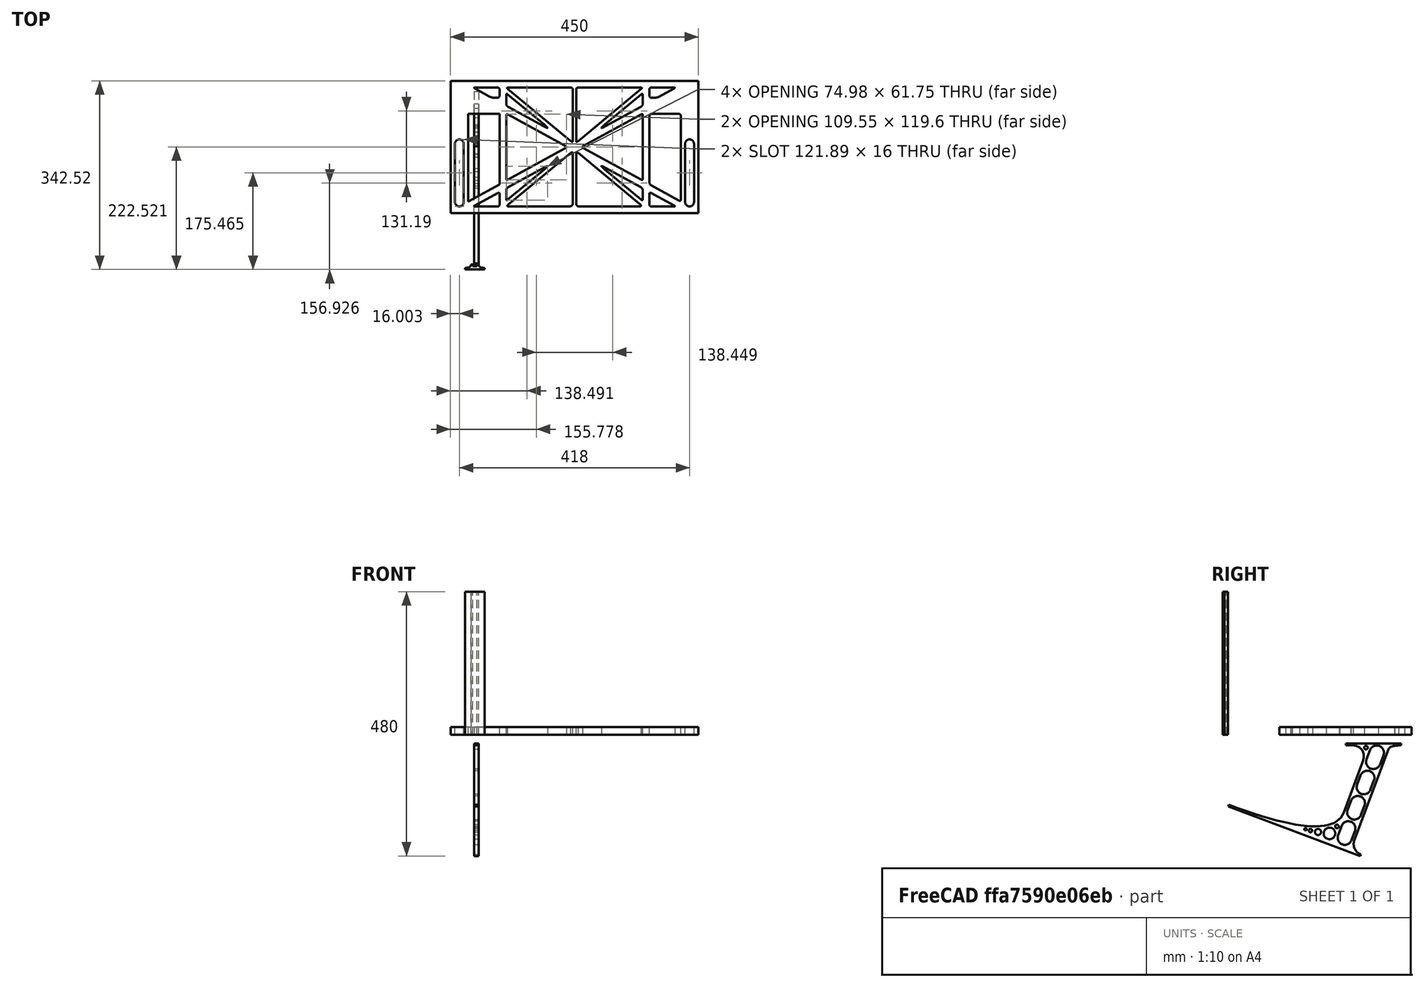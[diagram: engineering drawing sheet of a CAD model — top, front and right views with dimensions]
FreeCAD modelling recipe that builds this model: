
FCSTD DOCUMENT  (FreeCAD 0.19R0.19.2)
Label: laptopStand147FCStd
License: All rights reserved
LicenseURL: http://en.wikipedia.org/wiki/All_rights_reserved
objects: Sketcher::SketchObject×4, Part::Extrusion×3
note: 7 computed .brp shape members not serialized (recipe doc carries the construction recipe); baked Part::Feature solids carry a one-line shape summary decoded from their .brp

FEATURE [Sketcher::SketchObject] Sketch
  FullyConstrained = false
  sketch-geometry (349):
    g0: LineSegment StartX=-10.9272 StartY=-82.7794 StartZ=0 EndX=46.0728 EndY=-51.4823 EndZ=0
    g1: LineSegment StartX=-10.9272 StartY=76.4095 StartZ=0 EndX=-10.9272 EndY=-82.7794 EndZ=0
    g2: LineSegment StartX=46.0728 StartY=76.4095 StartZ=0 EndX=46.0728 EndY=-51.4823 EndZ=0
    g3: LineSegment StartX=-42.9272 StartY=136.221 StartZ=0 EndX=-42.9272 EndY=-103.779 EndZ=0
    g4: LineSegment StartX=407.073 StartY=136.221 StartZ=0 EndX=407.073 EndY=-103.779 EndZ=0
    g5: ArcOfCircle CenterX=-26.9272 CenterY=-83.7794 CenterZ=0 NormalX=0 NormalY=0 NormalZ=1 AngleXU=0 Radius=8 StartAngle=3.14159 EndAngle=6.28319
    g6: ArcOfCircle CenterX=391.073 CenterY=22.1087 CenterZ=0 NormalX=0 NormalY=0 NormalZ=1 AngleXU=0 Radius=8 StartAngle=-4.4e-15 EndAngle=3.14159
    g7: LineSegment StartX=399.073 StartY=22.1087 StartZ=0 EndX=399.073 EndY=-83.7794 EndZ=0
    g8: LineSegment StartX=383.073 StartY=22.1087 StartZ=0 EndX=383.073 EndY=-83.7794 EndZ=0
    g9: ArcOfCircle CenterX=391.073 CenterY=-83.7794 CenterZ=0 NormalX=0 NormalY=0 NormalZ=1 AngleXU=0 Radius=8 StartAngle=3.14159 EndAngle=6.28319
    g10: Circle CenterX=175.022 CenterY=27.0628 CenterZ=0 NormalX=0 NormalY=0 NormalZ=1 AngleXU=0 Radius=1
    g11: Circle CenterX=179.022 CenterY=24.8665 CenterZ=0 NormalX=0 NormalY=0 NormalZ=1 AngleXU=0 Radius=1
    g12: Circle CenterX=179.022 CenterY=27.0628 CenterZ=0 NormalX=0 NormalY=0 NormalZ=1 AngleXU=0 Radius=1
    g13: BSplineCurve PolesCount=3 KnotsCount=2 Degree=2 IsPeriodic=0
    g14: GeomPoint X=175.022 Y=27.0628 Z=0
    g15: GeomPoint X=179.022 Y=27.0628 Z=0
    g16: Circle CenterX=189.124 CenterY=27.0628 CenterZ=0 NormalX=0 NormalY=0 NormalZ=1 AngleXU=0 Radius=1
    g17: Circle CenterX=185.124 CenterY=24.8665 CenterZ=0 NormalX=0 NormalY=0 NormalZ=1 AngleXU=0 Radius=1
    g18: Circle CenterX=185.124 CenterY=27.0628 CenterZ=0 NormalX=0 NormalY=0 NormalZ=1 AngleXU=0 Radius=1
    g19: BSplineCurve PolesCount=3 KnotsCount=2 Degree=2 IsPeriodic=0
    g20: GeomPoint X=189.124 Y=27.0628 Z=0
    g21: GeomPoint X=185.124 Y=27.0628 Z=0
    g22: Circle CenterX=175.022 CenterY=5.37834 CenterZ=0 NormalX=0 NormalY=0 NormalZ=1 AngleXU=0 Radius=1
    g23: Circle CenterX=179.022 CenterY=7.57463 CenterZ=0 NormalX=0 NormalY=0 NormalZ=1 AngleXU=0 Radius=1
    g24: Circle CenterX=179.022 CenterY=5.34704 CenterZ=0 NormalX=0 NormalY=0 NormalZ=1 AngleXU=0 Radius=1
    g25: BSplineCurve PolesCount=3 KnotsCount=2 Degree=2 IsPeriodic=0
    g26: GeomPoint X=175.022 Y=5.37834 Z=0
    g27: GeomPoint X=179.022 Y=5.34704 Z=0
    g28: Circle CenterX=189.124 CenterY=5.37834 CenterZ=0 NormalX=0 NormalY=0 NormalZ=1 AngleXU=0 Radius=1
    g29: Circle CenterX=185.124 CenterY=7.57463 CenterZ=0 NormalX=0 NormalY=0 NormalZ=1 AngleXU=0 Radius=1
    g30: Circle CenterX=185.124 CenterY=5.34704 CenterZ=0 NormalX=0 NormalY=0 NormalZ=1 AngleXU=0 Radius=1
    g31: BSplineCurve PolesCount=3 KnotsCount=2 Degree=2 IsPeriodic=0
    g32: GeomPoint X=189.124 Y=5.37834 Z=0
    g33: GeomPoint X=185.124 Y=5.34704 Z=0
    g34: Circle CenterX=165.871 CenterY=18.1458 CenterZ=0 NormalX=0 NormalY=0 NormalZ=1 AngleXU=0 Radius=1
    g35: Circle CenterX=169.377 CenterY=16.2206 CenterZ=0 NormalX=0 NormalY=0 NormalZ=1 AngleXU=0 Radius=1
    g36: Circle CenterX=165.871 CenterY=14.2954 CenterZ=0 NormalX=0 NormalY=0 NormalZ=1 AngleXU=0 Radius=1
    g37: BSplineCurve PolesCount=3 KnotsCount=2 Degree=2 IsPeriodic=0
    g38: GeomPoint X=165.871 Y=18.1458 Z=0
    g39: GeomPoint X=165.871 Y=14.2954 Z=0
    g40: Circle CenterX=198.275 CenterY=18.1458 CenterZ=0 NormalX=0 NormalY=0 NormalZ=1 AngleXU=0 Radius=1
    g41: Circle CenterX=194.768 CenterY=16.2206 CenterZ=0 NormalX=0 NormalY=0 NormalZ=1 AngleXU=0 Radius=1
    g42: Circle CenterX=198.275 CenterY=14.2954 CenterZ=0 NormalX=0 NormalY=0 NormalZ=1 AngleXU=0 Radius=1
    g43: BSplineCurve PolesCount=3 KnotsCount=2 Degree=2 IsPeriodic=0
    g44: GeomPoint X=198.275 Y=18.1458 Z=0
    g45: GeomPoint X=198.275 Y=14.2954 Z=0
    g46: LineSegment StartX=407.073 StartY=-103.779 StartZ=0 EndX=-42.9272 EndY=-103.779 EndZ=0
    g47: LineSegment StartX=407.073 StartY=136.221 StartZ=0 EndX=-42.9272 EndY=136.221 EndZ=0
    g48: LineSegment StartX=46.0728 StartY=76.4095 StartZ=0 EndX=-10.9272 EndY=76.4095 EndZ=0
    g49: Circle CenterX=125.607 CenterY=54.1951 CenterZ=0 NormalX=0 NormalY=0 NormalZ=1 AngleXU=0 Radius=1
    g50: Circle CenterX=139.632 CenterY=46.4944 CenterZ=0 NormalX=0 NormalY=0 NormalZ=1 AngleXU=0 Radius=1
    g51: Circle CenterX=127.326 CenterY=56.7187 CenterZ=0 NormalX=0 NormalY=0 NormalZ=1 AngleXU=0 Radius=1
    g52: BSplineCurve PolesCount=3 KnotsCount=2 Degree=2 IsPeriodic=0
    g53: GeomPoint X=125.607 Y=54.1951 Z=0
    g54: GeomPoint X=127.326 Y=56.7187 Z=0
    g55: Circle CenterX=236.821 CenterY=56.7187 CenterZ=0 NormalX=0 NormalY=0 NormalZ=1 AngleXU=0 Radius=1
    g56: Circle CenterX=224.513 CenterY=46.4944 CenterZ=0 NormalX=0 NormalY=0 NormalZ=1 AngleXU=0 Radius=1
    g57: Circle CenterX=238.538 CenterY=54.1951 CenterZ=0 NormalX=0 NormalY=0 NormalZ=1 AngleXU=0 Radius=1
    g58: BSplineCurve PolesCount=3 KnotsCount=2 Degree=2 IsPeriodic=0
    g59: GeomPoint X=236.821 Y=56.7187 Z=0
    g60: GeomPoint X=238.538 Y=54.1951 Z=0
    g61: Circle CenterX=238.538 CenterY=-21.7539 CenterZ=0 NormalX=0 NormalY=0 NormalZ=1 AngleXU=0 Radius=1
    g62: Circle CenterX=224.513 CenterY=-14.0532 CenterZ=0 NormalX=0 NormalY=0 NormalZ=1 AngleXU=0 Radius=1
    g63: Circle CenterX=236.821 CenterY=-24.2775 CenterZ=0 NormalX=0 NormalY=0 NormalZ=1 AngleXU=0 Radius=1
    g64: BSplineCurve PolesCount=3 KnotsCount=2 Degree=2 IsPeriodic=0
    g65: GeomPoint X=238.538 Y=-21.7539 Z=0
    g66: GeomPoint X=236.821 Y=-24.2775 Z=0
    g67: Circle CenterX=125.607 CenterY=-21.7539 CenterZ=0 NormalX=0 NormalY=0 NormalZ=1 AngleXU=0 Radius=1
    g68: Circle CenterX=139.632 CenterY=-14.0532 CenterZ=0 NormalX=0 NormalY=0 NormalZ=1 AngleXU=0 Radius=1
    g69: Circle CenterX=127.325 CenterY=-24.2775 CenterZ=0 NormalX=0 NormalY=0 NormalZ=1 AngleXU=0 Radius=1
    g70: BSplineCurve PolesCount=3 KnotsCount=2 Degree=2 IsPeriodic=0
    g71: GeomPoint X=125.607 Y=-21.7539 Z=0
    g72: GeomPoint X=127.325 Y=-24.2775 Z=0
    g73: Circle CenterX=302.996 CenterY=111.695 CenterZ=0 NormalX=0 NormalY=0 NormalZ=1 AngleXU=0 Radius=1
    g74: Circle CenterX=306.073 CenterY=114.251 CenterZ=0 NormalX=0 NormalY=0 NormalZ=1 AngleXU=0 Radius=1
    g75: Circle CenterX=306.073 CenterY=110.251 CenterZ=0 NormalX=0 NormalY=0 NormalZ=1 AngleXU=0 Radius=1
    g76: BSplineCurve PolesCount=3 KnotsCount=2 Degree=2 IsPeriodic=0
    g77: GeomPoint X=302.996 Y=111.695 Z=0
    g78: GeomPoint X=306.073 Y=110.251 Z=0
    g79: Circle CenterX=306.073 CenterY=95.2763 CenterZ=0 NormalX=0 NormalY=0 NormalZ=1 AngleXU=0 Radius=1
    g80: Circle CenterX=306.073 CenterY=91.2763 CenterZ=0 NormalX=0 NormalY=0 NormalZ=1 AngleXU=0 Radius=1
    g81: Circle CenterX=302.567 CenterY=89.3511 CenterZ=0 NormalX=0 NormalY=0 NormalZ=1 AngleXU=0 Radius=1
    g82: BSplineCurve PolesCount=3 KnotsCount=2 Degree=2 IsPeriodic=0
    g83: GeomPoint X=306.073 Y=95.2763 Z=0
    g84: GeomPoint X=302.567 Y=89.3511 Z=0
    g85: LineSegment StartX=306.073 StartY=110.251 StartZ=0 EndX=306.073 EndY=95.2763 EndZ=0
    g86: LineSegment StartX=302.996 StartY=111.695 StartZ=0 EndX=236.821 EndY=56.7187 EndZ=0
    g87: LineSegment StartX=238.538 StartY=54.1951 StartZ=0 EndX=302.567 EndY=89.3511 EndZ=0
    g88: Circle CenterX=61.1496 CenterY=111.695 CenterZ=0 NormalX=0 NormalY=0 NormalZ=1 AngleXU=0 Radius=1
    g89: Circle CenterX=58.0728 CenterY=114.251 CenterZ=0 NormalX=0 NormalY=0 NormalZ=1 AngleXU=0 Radius=1
    g90: Circle CenterX=58.0728 CenterY=110.251 CenterZ=0 NormalX=0 NormalY=0 NormalZ=1 AngleXU=0 Radius=1
    g91: BSplineCurve PolesCount=3 KnotsCount=2 Degree=2 IsPeriodic=0
    g92: GeomPoint X=61.1496 Y=111.695 Z=0
    g93: GeomPoint X=58.0728 Y=110.251 Z=0
    g94: Circle CenterX=61.5791 CenterY=89.3511 CenterZ=0 NormalX=0 NormalY=0 NormalZ=1 AngleXU=0 Radius=1
    g95: Circle CenterX=58.0728 CenterY=91.2763 CenterZ=0 NormalX=0 NormalY=0 NormalZ=1 AngleXU=0 Radius=1
    g96: Circle CenterX=58.0728 CenterY=95.2763 CenterZ=0 NormalX=0 NormalY=0 NormalZ=1 AngleXU=0 Radius=1
    g97: BSplineCurve PolesCount=3 KnotsCount=2 Degree=2 IsPeriodic=0
    g98: GeomPoint X=61.5791 Y=89.3511 Z=0
    g99: GeomPoint X=58.0728 Y=95.2763 Z=0
    g100: LineSegment StartX=58.0728 StartY=110.251 StartZ=0 EndX=58.0728 EndY=95.2763 EndZ=0
    g101: LineSegment StartX=61.1496 StartY=111.695 StartZ=0 EndX=127.326 EndY=56.7187 EndZ=0
    g102: LineSegment StartX=125.607 StartY=54.1951 StartZ=0 EndX=61.5791 EndY=89.3511 EndZ=0
    g103: Circle CenterX=61.5791 CenterY=-56.9099 CenterZ=0 NormalX=0 NormalY=0 NormalZ=1 AngleXU=0 Radius=1
    g104: Circle CenterX=58.0728 CenterY=-58.8351 CenterZ=0 NormalX=0 NormalY=0 NormalZ=1 AngleXU=0 Radius=1
    g105: Circle CenterX=58.0728 CenterY=-62.8351 CenterZ=0 NormalX=0 NormalY=0 NormalZ=1 AngleXU=0 Radius=1
    g106: BSplineCurve PolesCount=3 KnotsCount=2 Degree=2 IsPeriodic=0
    g107: GeomPoint X=61.5791 Y=-56.9099 Z=0
    g108: GeomPoint X=58.0728 Y=-62.8351 Z=0
    g109: Circle CenterX=58.0728 CenterY=-77.8102 CenterZ=0 NormalX=0 NormalY=0 NormalZ=1 AngleXU=0 Radius=1
    g110: Circle CenterX=58.0728 CenterY=-81.8102 CenterZ=0 NormalX=0 NormalY=0 NormalZ=1 AngleXU=0 Radius=1
    g111: Circle CenterX=61.1496 CenterY=-79.2541 CenterZ=0 NormalX=0 NormalY=0 NormalZ=1 AngleXU=0 Radius=1
    g112: BSplineCurve PolesCount=3 KnotsCount=2 Degree=2 IsPeriodic=0
    g113: GeomPoint X=58.0728 Y=-77.8102 Z=0
    g114: GeomPoint X=61.1496 Y=-79.2541 Z=0
    g115: LineSegment StartX=58.0728 StartY=-62.8351 StartZ=0 EndX=58.0728 EndY=-77.8102 EndZ=0
    g116: LineSegment StartX=61.1496 StartY=-79.2541 StartZ=0 EndX=127.325 EndY=-24.2775 EndZ=0
    g117: LineSegment StartX=125.607 StartY=-21.7539 StartZ=0 EndX=61.5791 EndY=-56.9099 EndZ=0
    g118: Circle CenterX=302.567 CenterY=-56.9099 CenterZ=0 NormalX=0 NormalY=0 NormalZ=1 AngleXU=0 Radius=1
    g119: Circle CenterX=306.073 CenterY=-58.8351 CenterZ=0 NormalX=0 NormalY=0 NormalZ=1 AngleXU=0 Radius=1
    g120: Circle CenterX=306.073 CenterY=-62.8351 CenterZ=0 NormalX=0 NormalY=0 NormalZ=1 AngleXU=0 Radius=1
    g121: BSplineCurve PolesCount=3 KnotsCount=2 Degree=2 IsPeriodic=0
    g122: GeomPoint X=302.567 Y=-56.9099 Z=0
    g123: GeomPoint X=306.073 Y=-62.8351 Z=0
    g124: Circle CenterX=302.996 CenterY=-79.2541 CenterZ=0 NormalX=0 NormalY=0 NormalZ=1 AngleXU=0 Radius=1
    g125: Circle CenterX=306.073 CenterY=-81.8102 CenterZ=0 NormalX=0 NormalY=0 NormalZ=1 AngleXU=0 Radius=1
    g126: Circle CenterX=306.073 CenterY=-77.8102 CenterZ=0 NormalX=0 NormalY=0 NormalZ=1 AngleXU=0 Radius=1
    g127: BSplineCurve PolesCount=3 KnotsCount=2 Degree=2 IsPeriodic=0
    g128: GeomPoint X=302.996 Y=-79.2541 Z=0
    g129: GeomPoint X=306.073 Y=-77.8102 Z=0
    g130: LineSegment StartX=306.073 StartY=-62.8351 StartZ=0 EndX=306.073 EndY=-77.8102 EndZ=0
    g131: LineSegment StartX=302.996 StartY=-79.2541 StartZ=0 EndX=236.821 EndY=-24.2775 EndZ=0
    g132: LineSegment StartX=238.538 StartY=-21.7539 StartZ=0 EndX=302.567 EndY=-56.9099 EndZ=0
    g133: Circle CenterX=61.6457 CenterY=-88.8112 CenterZ=0 NormalX=0 NormalY=0 NormalZ=1 AngleXU=0 Radius=1
    g134: Circle CenterX=58.0728 CenterY=-91.7794 CenterZ=0 NormalX=0 NormalY=0 NormalZ=1 AngleXU=0 Radius=1
    g135: Circle CenterX=63.9135 CenterY=-91.7794 CenterZ=0 NormalX=0 NormalY=0 NormalZ=1 AngleXU=0 Radius=1
    g136: BSplineCurve PolesCount=3 KnotsCount=2 Degree=2 IsPeriodic=0
    g137: GeomPoint X=61.6457 Y=-88.8112 Z=0
    g138: GeomPoint X=63.9135 Y=-91.7794 Z=0
    g139: Circle CenterX=179.022 CenterY=-85.8163 CenterZ=0 NormalX=0 NormalY=0 NormalZ=1 AngleXU=0 Radius=1
    g140: Circle CenterX=179.022 CenterY=-91.7794 CenterZ=0 NormalX=0 NormalY=0 NormalZ=1 AngleXU=0 Radius=1
    g141: Circle CenterX=171.895 CenterY=-91.7794 CenterZ=0 NormalX=0 NormalY=0 NormalZ=1 AngleXU=0 Radius=1
    g142: BSplineCurve PolesCount=3 KnotsCount=2 Degree=2 IsPeriodic=0
    g143: GeomPoint X=179.022 Y=-85.8163 Z=0
    g144: GeomPoint X=171.895 Y=-91.7794 Z=0
    g145: Circle CenterX=185.124 CenterY=-86.2028 CenterZ=0 NormalX=0 NormalY=0 NormalZ=1 AngleXU=0 Radius=1
    g146: Circle CenterX=185.124 CenterY=-91.7794 CenterZ=0 NormalX=0 NormalY=0 NormalZ=1 AngleXU=0 Radius=1
    g147: Circle CenterX=191.747 CenterY=-91.7794 CenterZ=0 NormalX=0 NormalY=0 NormalZ=1 AngleXU=0 Radius=1
    g148: BSplineCurve PolesCount=3 KnotsCount=2 Degree=2 IsPeriodic=0
    g149: GeomPoint X=185.124 Y=-86.2028 Z=0
    g150: GeomPoint X=191.747 Y=-91.7794 Z=0
    g151: Circle CenterX=299.888 CenterY=-86.6413 CenterZ=0 NormalX=0 NormalY=0 NormalZ=1 AngleXU=0 Radius=1
    g152: Circle CenterX=306.073 CenterY=-91.7794 CenterZ=0 NormalX=0 NormalY=0 NormalZ=1 AngleXU=0 Radius=1
    g153: Circle CenterX=298.776 CenterY=-91.7794 CenterZ=0 NormalX=0 NormalY=0 NormalZ=1 AngleXU=0 Radius=1
    g154: BSplineCurve PolesCount=3 KnotsCount=2 Degree=2 IsPeriodic=0
    g155: GeomPoint X=299.888 Y=-86.6413 Z=0
    g156: GeomPoint X=298.776 Y=-91.7794 Z=0
    g157: LineSegment StartX=189.124 StartY=5.37834 StartZ=0 EndX=299.888 EndY=-86.6413 EndZ=0
    g158: LineSegment StartX=298.776 StartY=-91.7794 StartZ=0 EndX=191.747 EndY=-91.7794 EndZ=0
    g159: LineSegment StartX=185.124 StartY=-86.2028 StartZ=0 EndX=185.124 EndY=5.34704 EndZ=0
    g160: LineSegment StartX=179.022 StartY=5.34704 StartZ=0 EndX=179.022 EndY=-85.8163 EndZ=0
    g161: LineSegment StartX=171.895 StartY=-91.7794 StartZ=0 EndX=63.9135 EndY=-91.7794 EndZ=0
    g162: LineSegment StartX=61.6457 StartY=-88.8112 StartZ=0 EndX=175.022 EndY=5.37834 EndZ=0
    g163: Circle CenterX=302.073 CenterY=124.221 CenterZ=0 NormalX=0 NormalY=0 NormalZ=1 AngleXU=0 Radius=1
    g164: Circle CenterX=306.073 CenterY=124.221 CenterZ=0 NormalX=0 NormalY=0 NormalZ=1 AngleXU=0 Radius=1
    g165: Circle CenterX=302.996 CenterY=121.665 CenterZ=0 NormalX=0 NormalY=0 NormalZ=1 AngleXU=0 Radius=1
    g166: BSplineCurve PolesCount=3 KnotsCount=2 Degree=2 IsPeriodic=0
    g167: GeomPoint X=302.073 Y=124.221 Z=0
    g168: GeomPoint X=302.996 Y=121.665 Z=0
    g169: Circle CenterX=189.124 CenterY=124.221 CenterZ=0 NormalX=0 NormalY=0 NormalZ=1 AngleXU=0 Radius=1
    g170: Circle CenterX=185.124 CenterY=124.221 CenterZ=0 NormalX=0 NormalY=0 NormalZ=1 AngleXU=0 Radius=1
    g171: Circle CenterX=185.124 CenterY=120.221 CenterZ=0 NormalX=0 NormalY=0 NormalZ=1 AngleXU=0 Radius=1
    g172: BSplineCurve PolesCount=3 KnotsCount=2 Degree=2 IsPeriodic=0
    g173: GeomPoint X=189.124 Y=124.221 Z=0
    g174: GeomPoint X=185.124 Y=120.221 Z=0
    g175: Circle CenterX=175.022 CenterY=124.221 CenterZ=0 NormalX=0 NormalY=0 NormalZ=1 AngleXU=0 Radius=1
    g176: Circle CenterX=179.022 CenterY=124.221 CenterZ=0 NormalX=0 NormalY=0 NormalZ=1 AngleXU=0 Radius=1
    g177: Circle CenterX=179.022 CenterY=120.221 CenterZ=0 NormalX=0 NormalY=0 NormalZ=1 AngleXU=0 Radius=1
    g178: BSplineCurve PolesCount=3 KnotsCount=2 Degree=2 IsPeriodic=0
    g179: GeomPoint X=175.022 Y=124.221 Z=0
    g180: GeomPoint X=179.022 Y=120.221 Z=0
    g181: Circle CenterX=62.0728 CenterY=124.221 CenterZ=0 NormalX=0 NormalY=0 NormalZ=1 AngleXU=0 Radius=1
    g182: Circle CenterX=58.0728 CenterY=124.221 CenterZ=0 NormalX=0 NormalY=0 NormalZ=1 AngleXU=0 Radius=1
    g183: Circle CenterX=61.1496 CenterY=121.665 CenterZ=0 NormalX=0 NormalY=0 NormalZ=1 AngleXU=0 Radius=1
    g184: BSplineCurve PolesCount=3 KnotsCount=2 Degree=2 IsPeriodic=0
    g185: GeomPoint X=62.0728 Y=124.221 Z=0
    g186: GeomPoint X=61.1496 Y=121.665 Z=0
    g187: LineSegment StartX=62.0728 StartY=124.221 StartZ=0 EndX=175.022 EndY=124.221 EndZ=0
    g188: LineSegment StartX=179.022 StartY=120.221 StartZ=0 EndX=179.022 EndY=27.0628 EndZ=0
    g189: LineSegment StartX=185.124 StartY=27.0628 StartZ=0 EndX=185.124 EndY=120.221 EndZ=0
    g190: LineSegment StartX=189.124 StartY=124.221 StartZ=0 EndX=302.073 EndY=124.221 EndZ=0
    g191: LineSegment StartX=302.996 StartY=121.665 StartZ=0 EndX=189.124 EndY=27.0628 EndZ=0
    g192: LineSegment StartX=175.022 StartY=27.0628 StartZ=0 EndX=61.1496 EndY=121.665 EndZ=0
    g193: Circle CenterX=61.5791 CenterY=75.4095 CenterZ=0 NormalX=0 NormalY=0 NormalZ=1 AngleXU=0 Radius=1
    g194: Circle CenterX=58.0728 CenterY=77.3346 CenterZ=0 NormalX=0 NormalY=0 NormalZ=1 AngleXU=0 Radius=1
    g195: Circle CenterX=58.0728 CenterY=73.3346 CenterZ=0 NormalX=0 NormalY=0 NormalZ=1 AngleXU=0 Radius=1
    g196: BSplineCurve PolesCount=3 KnotsCount=2 Degree=2 IsPeriodic=0
    g197: GeomPoint X=61.5791 Y=75.4095 Z=0
    g198: GeomPoint X=58.0728 Y=73.3346 Z=0
    g199: Circle CenterX=58.0728 CenterY=-40.8935 CenterZ=0 NormalX=0 NormalY=0 NormalZ=1 AngleXU=0 Radius=1
    g200: Circle CenterX=58.0728 CenterY=-44.8935 CenterZ=0 NormalX=0 NormalY=0 NormalZ=1 AngleXU=0 Radius=1
    g201: Circle CenterX=61.5791 CenterY=-42.9683 CenterZ=0 NormalX=0 NormalY=0 NormalZ=1 AngleXU=0 Radius=1
    g202: BSplineCurve PolesCount=3 KnotsCount=2 Degree=2 IsPeriodic=0
    g203: GeomPoint X=58.0728 Y=-40.8935 Z=0
    g204: GeomPoint X=61.5791 Y=-42.9683 Z=0
    g205: LineSegment StartX=61.5791 StartY=-42.9683 StartZ=0 EndX=165.871 EndY=14.2954 EndZ=0
    g206: LineSegment StartX=165.871 StartY=18.1458 StartZ=0 EndX=61.5791 EndY=75.4095 EndZ=0
    g207: LineSegment StartX=58.0728 StartY=73.3346 StartZ=0 EndX=58.0728 EndY=-40.8935 EndZ=0
    g208: Circle CenterX=302.567 CenterY=-42.9683 CenterZ=0 NormalX=0 NormalY=0 NormalZ=1 AngleXU=0 Radius=1
    g209: Circle CenterX=306.073 CenterY=-44.8935 CenterZ=0 NormalX=0 NormalY=0 NormalZ=1 AngleXU=0 Radius=1
    g210: Circle CenterX=306.073 CenterY=-40.8935 CenterZ=0 NormalX=0 NormalY=0 NormalZ=1 AngleXU=0 Radius=1
    g211: BSplineCurve PolesCount=3 KnotsCount=2 Degree=2 IsPeriodic=0
    g212: GeomPoint X=302.567 Y=-42.9683 Z=0
    g213: GeomPoint X=306.073 Y=-40.8935 Z=0
    g214: Circle CenterX=306.073 CenterY=73.3346 CenterZ=0 NormalX=0 NormalY=0 NormalZ=1 AngleXU=0 Radius=1
    g215: Circle CenterX=306.073 CenterY=77.3346 CenterZ=0 NormalX=0 NormalY=0 NormalZ=1 AngleXU=0 Radius=1
    g216: Circle CenterX=302.567 CenterY=75.4095 CenterZ=0 NormalX=0 NormalY=0 NormalZ=1 AngleXU=0 Radius=1
    g217: BSplineCurve PolesCount=3 KnotsCount=2 Degree=2 IsPeriodic=0
    g218: GeomPoint X=306.073 Y=73.3346 Z=0
    g219: GeomPoint X=302.567 Y=75.4095 Z=0
    g220: LineSegment StartX=302.567 StartY=-42.9683 StartZ=0 EndX=198.275 EndY=14.2954 EndZ=0
    g221: LineSegment StartX=198.275 StartY=18.1458 StartZ=0 EndX=302.567 EndY=75.4095 EndZ=0
    g222: LineSegment StartX=306.073 StartY=73.3346 StartZ=0 EndX=306.073 EndY=-40.8935 EndZ=0
    g223: LineSegment StartX=322.073 StartY=105.865 StartZ=0 EndX=328.643 EndY=105.865 EndZ=0
    g224: LineSegment StartX=318.073 StartY=120.221 StartZ=0 EndX=318.073 EndY=109.865 EndZ=0
    g225: LineSegment StartX=336.157 StartY=107.779 StartZ=0 EndX=362.567 EndY=122.294 EndZ=0
    g226: Circle CenterX=362.073 CenterY=124.221 CenterZ=0 NormalX=0 NormalY=0 NormalZ=1 AngleXU=0 Radius=1
    g227: Circle CenterX=366.073 CenterY=124.221 CenterZ=0 NormalX=0 NormalY=0 NormalZ=1 AngleXU=0 Radius=1
    g228: Circle CenterX=362.567 CenterY=122.294 CenterZ=0 NormalX=0 NormalY=0 NormalZ=1 AngleXU=0 Radius=1
    g229: BSplineCurve PolesCount=3 KnotsCount=2 Degree=2 IsPeriodic=0
    g230: GeomPoint X=362.073 Y=124.221 Z=0
    g231: GeomPoint X=362.567 Y=122.294 Z=0
    g232: Circle CenterX=322.073 CenterY=124.221 CenterZ=0 NormalX=0 NormalY=0 NormalZ=1 AngleXU=0 Radius=1
    g233: Circle CenterX=318.073 CenterY=124.221 CenterZ=0 NormalX=0 NormalY=0 NormalZ=1 AngleXU=0 Radius=1
    g234: Circle CenterX=318.073 CenterY=120.221 CenterZ=0 NormalX=0 NormalY=0 NormalZ=1 AngleXU=0 Radius=1
    g235: BSplineCurve PolesCount=3 KnotsCount=2 Degree=2 IsPeriodic=0
    g236: GeomPoint X=322.073 Y=124.221 Z=0
    g237: GeomPoint X=318.073 Y=120.221 Z=0
    g238: Circle CenterX=322.073 CenterY=105.865 CenterZ=0 NormalX=0 NormalY=0 NormalZ=1 AngleXU=0 Radius=1
    g239: Circle CenterX=318.073 CenterY=105.865 CenterZ=0 NormalX=0 NormalY=0 NormalZ=1 AngleXU=0 Radius=1
    g240: Circle CenterX=318.073 CenterY=109.865 CenterZ=0 NormalX=0 NormalY=0 NormalZ=1 AngleXU=0 Radius=1
    g241: BSplineCurve PolesCount=3 KnotsCount=2 Degree=2 IsPeriodic=0
    g242: GeomPoint X=322.073 Y=105.865 Z=0
    g243: GeomPoint X=318.073 Y=109.865 Z=0
    g244: Circle CenterX=336.157 CenterY=107.779 CenterZ=0 NormalX=0 NormalY=0 NormalZ=1 AngleXU=0 Radius=1
    g245: Circle CenterX=332.651 CenterY=105.853 CenterZ=0 NormalX=0 NormalY=0 NormalZ=1 AngleXU=0 Radius=1
    g246: Circle CenterX=328.643 CenterY=105.865 CenterZ=0 NormalX=0 NormalY=0 NormalZ=1 AngleXU=0 Radius=1
    g247: BSplineCurve PolesCount=3 KnotsCount=2 Degree=2 IsPeriodic=0
    g248: GeomPoint X=336.157 Y=107.779 Z=0
    g249: GeomPoint X=328.643 Y=105.865 Z=0
    g250: LineSegment StartX=322.073 StartY=124.221 StartZ=0 EndX=362.073 EndY=124.221 EndZ=0
    g251: Circle CenterX=371.567 CenterY=-80.8644 CenterZ=0 NormalX=0 NormalY=0 NormalZ=1 AngleXU=0 Radius=1
    g252: Circle CenterX=375.073 CenterY=-82.7896 CenterZ=0 NormalX=0 NormalY=0 NormalZ=1 AngleXU=0 Radius=1
    g253: Circle CenterX=375.073 CenterY=-78.7896 CenterZ=0 NormalX=0 NormalY=0 NormalZ=1 AngleXU=0 Radius=1
    g254: BSplineCurve PolesCount=3 KnotsCount=2 Degree=2 IsPeriodic=0
    g255: GeomPoint X=371.567 Y=-80.8644 Z=0
    g256: GeomPoint X=375.073 Y=-78.7896 Z=0
    g257: Circle CenterX=321.579 CenterY=-53.4075 CenterZ=0 NormalX=0 NormalY=0 NormalZ=1 AngleXU=0 Radius=1
    g258: Circle CenterX=318.073 CenterY=-51.4823 CenterZ=0 NormalX=0 NormalY=0 NormalZ=1 AngleXU=0 Radius=1
    g259: Circle CenterX=318.073 CenterY=-47.4805 CenterZ=0 NormalX=0 NormalY=0 NormalZ=1 AngleXU=0 Radius=1
    g260: BSplineCurve PolesCount=3 KnotsCount=2 Degree=2 IsPeriodic=0
    g261: GeomPoint X=321.579 Y=-53.4075 Z=0
    g262: GeomPoint X=318.073 Y=-47.4805 Z=0
    g263: LineSegment StartX=371.567 StartY=-80.8644 StartZ=0 EndX=321.579 EndY=-53.4075 EndZ=0
    g264: Circle CenterX=321.579 CenterY=-67.3492 CenterZ=0 NormalX=0 NormalY=0 NormalZ=1 AngleXU=0 Radius=1
    g265: Circle CenterX=318.073 CenterY=-65.424 CenterZ=0 NormalX=0 NormalY=0 NormalZ=1 AngleXU=0 Radius=1
    g266: Circle CenterX=318.073 CenterY=-69.424 CenterZ=0 NormalX=0 NormalY=0 NormalZ=1 AngleXU=0 Radius=1
    g267: BSplineCurve PolesCount=3 KnotsCount=2 Degree=2 IsPeriodic=0
    g268: GeomPoint X=321.579 Y=-67.3492 Z=0
    g269: GeomPoint X=318.073 Y=-69.424 Z=0
    g270: Circle CenterX=362.567 CenterY=-89.8542 CenterZ=0 NormalX=0 NormalY=0 NormalZ=1 AngleXU=0 Radius=1
    g271: Circle CenterX=366.073 CenterY=-91.7794 CenterZ=0 NormalX=0 NormalY=0 NormalZ=1 AngleXU=0 Radius=1
    g272: Circle CenterX=362.073 CenterY=-91.7794 CenterZ=0 NormalX=0 NormalY=0 NormalZ=1 AngleXU=0 Radius=1
    g273: BSplineCurve PolesCount=3 KnotsCount=2 Degree=2 IsPeriodic=0
    g274: GeomPoint X=362.567 Y=-89.8542 Z=0
    g275: GeomPoint X=362.073 Y=-91.7794 Z=0
    g276: Circle CenterX=322.073 CenterY=-91.7794 CenterZ=0 NormalX=0 NormalY=0 NormalZ=1 AngleXU=0 Radius=1
    g277: Circle CenterX=318.073 CenterY=-91.7794 CenterZ=0 NormalX=0 NormalY=0 NormalZ=1 AngleXU=0 Radius=1
    g278: Circle CenterX=318.073 CenterY=-87.7794 CenterZ=0 NormalX=0 NormalY=0 NormalZ=1 AngleXU=0 Radius=1
    g279: BSplineCurve PolesCount=3 KnotsCount=2 Degree=2 IsPeriodic=0
    g280: GeomPoint X=322.073 Y=-91.7794 Z=0
    g281: GeomPoint X=318.073 Y=-87.7794 Z=0
    g282: LineSegment StartX=362.567 StartY=-89.8542 StartZ=0 EndX=321.579 EndY=-67.3492 EndZ=0
    g283: LineSegment StartX=318.073 StartY=-69.424 StartZ=0 EndX=318.073 EndY=-87.7794 EndZ=0
    g284: LineSegment StartX=322.073 StartY=-91.7794 StartZ=0 EndX=362.073 EndY=-91.7794 EndZ=0
    g285: Circle CenterX=2.07281 CenterY=124.221 CenterZ=0 NormalX=0 NormalY=0 NormalZ=1 AngleXU=0 Radius=1
    g286: Circle CenterX=1.57905 CenterY=122.295 CenterZ=0 NormalX=0 NormalY=0 NormalZ=1 AngleXU=0 Radius=1
    g287: BSplineCurve PolesCount=3 KnotsCount=2 Degree=2 IsPeriodic=0
    g288: GeomPoint X=2.07281 Y=124.221 Z=0
    g289: GeomPoint X=1.57905 Y=122.295 Z=0
    g290: Circle CenterX=42.0728 CenterY=124.221 CenterZ=0 NormalX=0 NormalY=0 NormalZ=1 AngleXU=0 Radius=1
    g291: Circle CenterX=46.0728 CenterY=124.221 CenterZ=0 NormalX=0 NormalY=0 NormalZ=1 AngleXU=0 Radius=1
    g292: Circle CenterX=46.0728 CenterY=120.221 CenterZ=0 NormalX=0 NormalY=0 NormalZ=1 AngleXU=0 Radius=1
    g293: BSplineCurve PolesCount=3 KnotsCount=2 Degree=2 IsPeriodic=0
    g294: GeomPoint X=42.0728 Y=124.221 Z=0
    g295: GeomPoint X=46.0728 Y=120.221 Z=0
    g296: Circle CenterX=46.0728 CenterY=109.865 CenterZ=0 NormalX=0 NormalY=0 NormalZ=1 AngleXU=0 Radius=1
    g297: Circle CenterX=46.0728 CenterY=105.865 CenterZ=0 NormalX=0 NormalY=0 NormalZ=1 AngleXU=0 Radius=1
    g298: Circle CenterX=42.0728 CenterY=105.865 CenterZ=0 NormalX=0 NormalY=0 NormalZ=1 AngleXU=0 Radius=1
    g299: BSplineCurve PolesCount=3 KnotsCount=2 Degree=2 IsPeriodic=0
    g300: GeomPoint X=46.0728 Y=109.865 Z=0
    g301: GeomPoint X=42.0728 Y=105.865 Z=0
    g302: Circle CenterX=35.5028 CenterY=105.865 CenterZ=0 NormalX=0 NormalY=0 NormalZ=1 AngleXU=0 Radius=1
    g303: Circle CenterX=31.5028 CenterY=105.865 CenterZ=0 NormalX=0 NormalY=0 NormalZ=1 AngleXU=0 Radius=1
    g304: Circle CenterX=27.9965 CenterY=107.79 CenterZ=0 NormalX=0 NormalY=0 NormalZ=1 AngleXU=0 Radius=1
    g305: BSplineCurve PolesCount=3 KnotsCount=2 Degree=2 IsPeriodic=0
    g306: GeomPoint X=35.5028 Y=105.865 Z=0
    g307: GeomPoint X=27.9965 Y=107.79 Z=0
    g308: LineSegment StartX=2.07281 StartY=124.221 StartZ=0 EndX=42.0728 EndY=124.221 EndZ=0
    g309: LineSegment StartX=46.0728 StartY=120.221 StartZ=0 EndX=46.0728 EndY=109.865 EndZ=0
    g310: LineSegment StartX=42.0728 StartY=105.865 StartZ=0 EndX=35.5028 EndY=105.865 EndZ=0
    g311: LineSegment StartX=27.9965 StartY=107.79 StartZ=0 EndX=1.57905 EndY=122.295 EndZ=0
    g312: Circle CenterX=42.5666 CenterY=-67.3492 CenterZ=0 NormalX=0 NormalY=0 NormalZ=1 AngleXU=0 Radius=1
    g313: Circle CenterX=46.0728 CenterY=-65.424 CenterZ=0 NormalX=0 NormalY=0 NormalZ=1 AngleXU=0 Radius=1
    g314: Circle CenterX=46.0728 CenterY=-69.424 CenterZ=0 NormalX=0 NormalY=0 NormalZ=1 AngleXU=0 Radius=1
    g315: BSplineCurve PolesCount=3 KnotsCount=2 Degree=2 IsPeriodic=0
    g316: GeomPoint X=42.5666 Y=-67.3492 Z=0
    g317: GeomPoint X=46.0728 Y=-69.424 Z=0
    g318: Circle CenterX=46.0728 CenterY=-87.7794 CenterZ=0 NormalX=0 NormalY=0 NormalZ=1 AngleXU=0 Radius=1
    g319: Circle CenterX=46.0728 CenterY=-91.7794 CenterZ=0 NormalX=0 NormalY=0 NormalZ=1 AngleXU=0 Radius=1
    g320: Circle CenterX=42.0728 CenterY=-91.7794 CenterZ=0 NormalX=0 NormalY=0 NormalZ=1 AngleXU=0 Radius=1
    g321: BSplineCurve PolesCount=3 KnotsCount=2 Degree=2 IsPeriodic=0
    g322: GeomPoint X=46.0728 Y=-87.7794 Z=0
    g323: GeomPoint X=42.0728 Y=-91.7794 Z=0
    g324: Circle CenterX=2.07281 CenterY=-91.7794 CenterZ=0 NormalX=0 NormalY=0 NormalZ=1 AngleXU=0 Radius=1
    g325: Circle CenterX=-1.92719 CenterY=-91.7794 CenterZ=0 NormalX=0 NormalY=0 NormalZ=1 AngleXU=0 Radius=1
    g326: Circle CenterX=1.57905 CenterY=-89.8542 CenterZ=0 NormalX=0 NormalY=0 NormalZ=1 AngleXU=0 Radius=1
    g327: BSplineCurve PolesCount=3 KnotsCount=2 Degree=2 IsPeriodic=0
    g328: GeomPoint X=2.07281 Y=-91.7794 Z=0
    g329: GeomPoint X=1.57905 Y=-89.8542 Z=0
    g330: LineSegment StartX=2.07281 StartY=-91.7794 StartZ=0 EndX=42.0728 EndY=-91.7794 EndZ=0
    g331: LineSegment StartX=46.0728 StartY=-87.7794 StartZ=0 EndX=46.0728 EndY=-69.424 EndZ=0
    g332: LineSegment StartX=42.5666 StartY=-67.3492 StartZ=0 EndX=1.57905 EndY=-89.8542 EndZ=0
    g333: Circle CenterX=322.073 CenterY=76.4095 CenterZ=0 NormalX=0 NormalY=0 NormalZ=1 AngleXU=0 Radius=4
    g334: BSplineCurve PolesCount=3 KnotsCount=2 Degree=2 IsPeriodic=0
    g335: GeomPoint X=318.073 Y=72.4095 Z=0
    g336: GeomPoint X=322.073 Y=76.4095 Z=0
    g337: Circle CenterX=375.073 CenterY=72.4095 CenterZ=0 NormalX=0 NormalY=0 NormalZ=1 AngleXU=0 Radius=1
    g338: Circle CenterX=375.073 CenterY=76.4095 CenterZ=0 NormalX=0 NormalY=0 NormalZ=1 AngleXU=0 Radius=1
    g339: Circle CenterX=371.073 CenterY=76.4095 CenterZ=0 NormalX=0 NormalY=0 NormalZ=1 AngleXU=0 Radius=1
    g340: BSplineCurve PolesCount=3 KnotsCount=2 Degree=2 IsPeriodic=0
    g341: GeomPoint X=375.073 Y=72.4095 Z=0
    g342: GeomPoint X=371.073 Y=76.4095 Z=0
    g343: LineSegment StartX=322.073 StartY=76.4095 StartZ=0 EndX=371.073 EndY=76.4095 EndZ=0
    g344: LineSegment StartX=318.073 StartY=72.4095 StartZ=0 EndX=318.073 EndY=-47.4805 EndZ=0
    g345: LineSegment StartX=375.073 StartY=72.4095 StartZ=0 EndX=375.073 EndY=-78.7896 EndZ=0
    g346: ArcOfCircle CenterX=-26.9272 CenterY=22.1087 CenterZ=0 NormalX=0 NormalY=0 NormalZ=1 AngleXU=0 Radius=4 StartAngle=5e-16 EndAngle=3.14159
    g347: LineSegment StartX=-30.9272 StartY=22.1087 StartZ=0 EndX=-34.9272 EndY=-83.7794 EndZ=0
    g348: LineSegment StartX=-18.9272 StartY=-83.7794 StartZ=0 EndX=-22.9272 EndY=22.1087 EndZ=0
  constraints (572):
    c: Coincident(g0,g2)
    c: Block(g0)
    c: Block(g1)
    c: Vertical(g3)
    c: Vertical(g4)
    c: Block(g4)
    c: Block(g3)
    c: Tangent(g6,g7) = 1.5708
    c: Tangent(g7,g9) = 1.5708
    c: Equal(g6,g9)
    c: Coincident(g8,g6)
    c: Coincident(g8,g9)
    c: Block(g7)
    c: Block(g8)
    c: Weight(g10) = 1
    c: Equal(g10,g11)
    c: Equal(g10,g12)
    c: InternalAlignment(g10,g13)
    c: InternalAlignment(g11,g13)
    c: InternalAlignment(g12,g13)
    c: InternalAlignment(g14,g13)
    c: InternalAlignment(g15,g13)
    c: Weight(g16) = 1
    c: Equal(g16,g17)
    c: Equal(g16,g18)
    c: InternalAlignment(g16,g19)
    c: InternalAlignment(g17,g19)
    c: InternalAlignment(g18,g19)
    c: InternalAlignment(g20,g19)
    c: InternalAlignment(g21,g19)
    c: Block(g19)
    c: Block(g13)
    c: Weight(g22) = 1
    c: Equal(g22,g23)
    c: Equal(g22,g24)
    c: InternalAlignment(g22,g25)
    c: InternalAlignment(g23,g25)
    c: InternalAlignment(g24,g25)
    c: InternalAlignment(g26,g25)
    c: InternalAlignment(g27,g25)
    c: Weight(g28) = 1
    c: Equal(g28,g29)
    c: Equal(g28,g30)
    c: InternalAlignment(g28,g31)
    c: InternalAlignment(g29,g31)
    c: InternalAlignment(g30,g31)
    c: InternalAlignment(g32,g31)
    c: InternalAlignment(g33,g31)
    c: Block(g31)
    c: Block(g25)
    c: Weight(g34) = 1
    c: Equal(g34,g35)
    c: Equal(g34,g36)
    c: InternalAlignment(g34,g37)
    c: InternalAlignment(g35,g37)
    c: InternalAlignment(g36,g37)
    c: InternalAlignment(g38,g37)
    c: InternalAlignment(g39,g37)
    c: Weight(g40) = 1
    c: Equal(g40,g41)
    c: Equal(g40,g42)
    c: InternalAlignment(g40,g43)
    c: InternalAlignment(g41,g43)
    c: InternalAlignment(g42,g43)
    c: InternalAlignment(g44,g43)
    c: InternalAlignment(g45,g43)
    c: Block(g37)
    c: Block(g43)
    c: Coincident(g46,g4)
    c: Coincident(g46,g3)
    c: Horizontal(g46)
    c: Distance(g46) = 450
    c: Coincident(g47,g4)
    c: Coincident(g47,g3)
    c: Horizontal(g47)
    c: Horizontal(g48)
    c: Coincident(g2,g48)
    c: Block(g48)
    c: Coincident(g1,g48)
    c: Weight(g49) = 1
    c: Equal(g49,g50)
    c: Equal(g49,g51)
    c: InternalAlignment(g49,g52)
    c: InternalAlignment(g50,g52)
    c: InternalAlignment(g51,g52)
    c: InternalAlignment(g53,g52)
    c: InternalAlignment(g54,g52)
    c: Block(g52)
    c: Weight(g55) = 1
    c: Equal(g55,g56)
    c: Equal(g55,g57)
    c: InternalAlignment(g55,g58)
    c: InternalAlignment(g56,g58)
    c: InternalAlignment(g57,g58)
    c: InternalAlignment(g59,g58)
    c: InternalAlignment(g60,g58)
    c: Block(g58)
    c: Weight(g61) = 1
    c: Equal(g61,g62)
    c: Equal(g61,g63)
    c: InternalAlignment(g61,g64)
    c: InternalAlignment(g62,g64)
    c: InternalAlignment(g63,g64)
    c: InternalAlignment(g65,g64)
    c: InternalAlignment(g66,g64)
    c: Block(g64)
    c: Weight(g67) = 1
    c: Equal(g67,g68)
    c: Equal(g67,g69)
    c: InternalAlignment(g67,g70)
    c: InternalAlignment(g68,g70)
    c: InternalAlignment(g69,g70)
    c: InternalAlignment(g71,g70)
    c: InternalAlignment(g72,g70)
    c: Block(g70)
    c: Weight(g73) = 1
    c: Equal(g73,g74)
    c: Equal(g73,g75)
    c: InternalAlignment(g73,g76)
    c: InternalAlignment(g74,g76)
    c: InternalAlignment(g75,g76)
    c: InternalAlignment(g77,g76)
    c: InternalAlignment(g78,g76)
    c: Weight(g79) = 1
    c: Equal(g79,g80)
    c: Equal(g79,g81)
    c: InternalAlignment(g79,g82)
    c: InternalAlignment(g80,g82)
    c: InternalAlignment(g81,g82)
    c: InternalAlignment(g83,g82)
    c: InternalAlignment(g84,g82)
    c: Block(g76)
    c: Block(g82)
    c: Coincident(g85,g76)
    c: Coincident(g85,g82)
    c: Vertical(g85)
    c: Coincident(g86,g76)
    c: Coincident(g86,g58)
    c: Coincident(g87,g58)
    c: Coincident(g87,g82)
    c: Weight(g88) = 1
    c: Equal(g88,g89)
    c: Equal(g88,g90)
    c: InternalAlignment(g88,g91)
    c: InternalAlignment(g89,g91)
    c: InternalAlignment(g90,g91)
    c: InternalAlignment(g92,g91)
    c: InternalAlignment(g93,g91)
    c: Weight(g94) = 1
    c: Equal(g94,g95)
    c: Equal(g94,g96)
    c: InternalAlignment(g94,g97)
    c: InternalAlignment(g95,g97)
    c: InternalAlignment(g96,g97)
    c: InternalAlignment(g98,g97)
    c: InternalAlignment(g99,g97)
    c: Block(g91)
    c: Block(g97)
    c: Coincident(g100,g91)
    c: Coincident(g100,g97)
    c: Vertical(g100)
    c: Coincident(g101,g91)
    c: Coincident(g101,g52)
    c: Coincident(g102,g52)
    c: Coincident(g102,g97)
    c: Weight(g103) = 1
    c: Equal(g103,g104)
    c: Equal(g103,g105)
    c: InternalAlignment(g103,g106)
    c: InternalAlignment(g104,g106)
    c: InternalAlignment(g105,g106)
    c: InternalAlignment(g107,g106)
    c: InternalAlignment(g108,g106)
    c: Weight(g109) = 1
    c: Equal(g109,g110)
    c: Equal(g109,g111)
    c: InternalAlignment(g109,g112)
    c: InternalAlignment(g110,g112)
    c: InternalAlignment(g111,g112)
    c: InternalAlignment(g113,g112)
    c: InternalAlignment(g114,g112)
    c: Block(g106)
    c: Block(g112)
    c: Coincident(g115,g106)
    c: Coincident(g115,g112)
    c: Vertical(g115)
    c: Coincident(g116,g112)
    c: Coincident(g116,g70)
    c: Coincident(g117,g70)
    c: Coincident(g117,g106)
    c: Weight(g118) = 1
    c: Equal(g118,g119)
    c: Equal(g118,g120)
    c: InternalAlignment(g118,g121)
    c: InternalAlignment(g119,g121)
    c: InternalAlignment(g120,g121)
    c: InternalAlignment(g122,g121)
    c: InternalAlignment(g123,g121)
    c: Weight(g124) = 1
    c: Equal(g124,g125)
    c: Equal(g124,g126)
    c: InternalAlignment(g124,g127)
    c: InternalAlignment(g125,g127)
    c: InternalAlignment(g126,g127)
    c: InternalAlignment(g128,g127)
    c: InternalAlignment(g129,g127)
    c: Block(g121)
    c: Block(g127)
    c: Coincident(g130,g121)
    c: Coincident(g130,g127)
    c: Vertical(g130)
    c: Coincident(g131,g127)
    c: Coincident(g131,g64)
    c: Coincident(g132,g64)
    c: Coincident(g132,g121)
    c: Weight(g133) = 1
    c: Equal(g133,g134)
    c: Equal(g133,g135)
    c: InternalAlignment(g133,g136)
    c: InternalAlignment(g134,g136)
    c: InternalAlignment(g135,g136)
    c: InternalAlignment(g137,g136)
    c: InternalAlignment(g138,g136)
    c: Weight(g139) = 1
    c: Equal(g139,g140)
    c: Equal(g139,g141)
    c: InternalAlignment(g139,g142)
    c: InternalAlignment(g140,g142)
    c: InternalAlignment(g141,g142)
    c: InternalAlignment(g143,g142)
    c: InternalAlignment(g144,g142)
    c: Weight(g145) = 1
    c: Equal(g145,g146)
    c: Equal(g145,g147)
    c: InternalAlignment(g145,g148)
    c: InternalAlignment(g146,g148)
    c: InternalAlignment(g147,g148)
    c: InternalAlignment(g149,g148)
    c: InternalAlignment(g150,g148)
    c: Weight(g151) = 1
    c: Equal(g151,g152)
    c: Equal(g151,g153)
    c: InternalAlignment(g151,g154)
    c: InternalAlignment(g152,g154)
    c: InternalAlignment(g153,g154)
    c: InternalAlignment(g155,g154)
    c: InternalAlignment(g156,g154)
    c: Block(g154)
    c: Block(g148)
    c: Block(g142)
    c: Block(g136)
    c: Coincident(g157,g31)
    c: Coincident(g157,g154)
    c: Coincident(g158,g154)
    c: Coincident(g158,g148)
    c: Horizontal(g158)
    c: Coincident(g159,g148)
    c: Coincident(g159,g31)
    c: Vertical(g159)
    c: Coincident(g160,g25)
    c: Coincident(g160,g142)
    c: Vertical(g160)
    c: Coincident(g161,g142)
    c: Coincident(g161,g136)
    c: Horizontal(g161)
    c: Coincident(g162,g136)
    c: Coincident(g162,g25)
    c: Weight(g163) = 1
    c: Equal(g163,g164)
    c: Equal(g163,g165)
    c: InternalAlignment(g163,g166)
    c: InternalAlignment(g164,g166)
    c: InternalAlignment(g165,g166)
    c: InternalAlignment(g167,g166)
    c: InternalAlignment(g168,g166)
    c: Weight(g169) = 1
    c: Equal(g169,g170)
    c: Equal(g169,g171)
    c: InternalAlignment(g169,g172)
    c: InternalAlignment(g170,g172)
    c: InternalAlignment(g171,g172)
    c: InternalAlignment(g173,g172)
    c: InternalAlignment(g174,g172)
    c: Weight(g175) = 1
    c: Equal(g175,g176)
    c: Equal(g175,g177)
    c: InternalAlignment(g175,g178)
    c: InternalAlignment(g176,g178)
    c: InternalAlignment(g177,g178)
    c: InternalAlignment(g179,g178)
    c: InternalAlignment(g180,g178)
    c: Weight(g181) = 1
    c: Equal(g181,g182)
    c: Equal(g181,g183)
    c: InternalAlignment(g181,g184)
    c: InternalAlignment(g182,g184)
    c: InternalAlignment(g183,g184)
    c: InternalAlignment(g185,g184)
    c: InternalAlignment(g186,g184)
    c: Block(g184)
    c: Block(g178)
    c: Block(g172)
    c: Block(g166)
    c: Coincident(g187,g184)
    c: Coincident(g187,g178)
    c: Horizontal(g187)
    c: Coincident(g188,g178)
    c: Coincident(g188,g13)
    c: Vertical(g188)
    c: Coincident(g189,g19)
    c: Coincident(g189,g172)
    c: Vertical(g189)
    c: Coincident(g190,g172)
    c: Coincident(g190,g166)
    c: Horizontal(g190)
    c: Coincident(g191,g166)
    c: Coincident(g191,g19)
    c: Coincident(g192,g13)
    c: Weight(g193) = 1
    c: Equal(g193,g194)
    c: Equal(g193,g195)
    c: InternalAlignment(g193,g196)
    c: InternalAlignment(g194,g196)
    c: InternalAlignment(g195,g196)
    c: InternalAlignment(g197,g196)
    c: InternalAlignment(g198,g196)
    c: Weight(g199) = 1
    c: Equal(g199,g200)
    c: Equal(g199,g201)
    c: InternalAlignment(g199,g202)
    c: InternalAlignment(g200,g202)
    c: InternalAlignment(g201,g202)
    c: InternalAlignment(g203,g202)
    c: InternalAlignment(g204,g202)
    c: Block(g202)
    c: Block(g196)
    c: Coincident(g205,g202)
    c: Coincident(g205,g37)
    c: Coincident(g206,g37)
    c: Coincident(g206,g196)
    c: Coincident(g207,g196)
    c: Coincident(g207,g202)
    c: Vertical(g207)
    c: Weight(g208) = 1
    c: Equal(g208,g209)
    c: Equal(g208,g210)
    c: InternalAlignment(g208,g211)
    c: InternalAlignment(g209,g211)
    c: InternalAlignment(g210,g211)
    c: InternalAlignment(g212,g211)
    c: InternalAlignment(g213,g211)
    c: Weight(g214) = 1
    c: Equal(g214,g215)
    c: Equal(g214,g216)
    c: InternalAlignment(g214,g217)
    c: InternalAlignment(g215,g217)
    c: InternalAlignment(g216,g217)
    c: InternalAlignment(g218,g217)
    c: InternalAlignment(g219,g217)
    c: Block(g217)
    c: Block(g211)
    c: Coincident(g220,g211)
    c: Coincident(g220,g43)
    c: Coincident(g221,g43)
    c: Coincident(g221,g217)
    c: Coincident(g222,g217)
    c: Coincident(g222,g211)
    c: Vertical(g222)
    c: Horizontal(g223)
    c: Block(g223)
    c: Vertical(g224)
    c: Block(g224)
    c: Block(g225)
    c: Weight(g226) = 1
    c: Equal(g226,g227)
    c: Equal(g226,g228)
    c: InternalAlignment(g226,g229)
    c: InternalAlignment(g227,g229)
    c: InternalAlignment(g228,g229)
    c: InternalAlignment(g230,g229)
    c: InternalAlignment(g231,g229)
    c: Weight(g232) = 1
    c: Equal(g232,g233)
    c: Equal(g232,g234)
    c: InternalAlignment(g232,g235)
    c: InternalAlignment(g233,g235)
    c: InternalAlignment(g234,g235)
    c: InternalAlignment(g236,g235)
    c: InternalAlignment(g237,g235)
    c: Weight(g238) = 1
    c: Equal(g238,g239)
    c: Equal(g238,g240)
    c: InternalAlignment(g238,g241)
    c: InternalAlignment(g239,g241)
    c: InternalAlignment(g240,g241)
    c: InternalAlignment(g242,g241)
    c: InternalAlignment(g243,g241)
    c: Weight(g244) = 1
    c: Equal(g244,g245)
    c: Equal(g244,g246)
    c: InternalAlignment(g244,g247)
    c: InternalAlignment(g245,g247)
    c: InternalAlignment(g246,g247)
    c: InternalAlignment(g248,g247)
    c: InternalAlignment(g249,g247)
    c: Block(g229)
    c: Block(g235)
    c: Block(g241)
    c: Block(g247)
    c: Coincident(g250,g235)
    c: Coincident(g250,g229)
    c: Horizontal(g250)
    c: Block(g192)
    c: Weight(g251) = 1
    c: Equal(g251,g252)
    c: Equal(g251,g253)
    c: InternalAlignment(g251,g254)
    c: InternalAlignment(g252,g254)
    c: InternalAlignment(g253,g254)
    c: InternalAlignment(g255,g254)
    c: InternalAlignment(g256,g254)
    c: Weight(g257) = 1
    c: Equal(g257,g258)
    c: Equal(g257,g259)
    c: InternalAlignment(g257,g260)
    c: InternalAlignment(g258,g260)
    c: InternalAlignment(g259,g260)
    c: InternalAlignment(g261,g260)
    c: InternalAlignment(g262,g260)
    c: Block(g254)
    c: Block(g260)
    c: Coincident(g263,g254)
    c: Coincident(g263,g260)
    c: Weight(g264) = 1
    c: Equal(g264,g265)
    c: Equal(g264,g266)
    c: InternalAlignment(g264,g267)
    c: InternalAlignment(g265,g267)
    c: InternalAlignment(g266,g267)
    c: InternalAlignment(g268,g267)
    c: InternalAlignment(g269,g267)
    c: Weight(g270) = 1
    c: Equal(g270,g271)
    c: Equal(g270,g272)
    c: InternalAlignment(g270,g273)
    c: InternalAlignment(g271,g273)
    c: InternalAlignment(g272,g273)
    c: InternalAlignment(g274,g273)
    c: InternalAlignment(g275,g273)
    c: Weight(g276) = 1
    c: Equal(g276,g277)
    c: Equal(g276,g278)
    c: InternalAlignment(g276,g279)
    c: InternalAlignment(g277,g279)
    c: InternalAlignment(g278,g279)
    c: InternalAlignment(g280,g279)
    c: InternalAlignment(g281,g279)
    c: Block(g279)
    c: Block(g273)
    c: Block(g267)
    c: Coincident(g282,g273)
    c: Coincident(g282,g267)
    c: Coincident(g283,g267)
    c: Coincident(g283,g279)
    c: Vertical(g283)
    c: Coincident(g284,g279)
    c: Coincident(g284,g273)
    c: Horizontal(g284)
    c: Weight(g285) = 1
    c: Equal(g285,g286)
    c: InternalAlignment(g285,g287)
    c: InternalAlignment(g286,g287)
    c: InternalAlignment(g288,g287)
    c: InternalAlignment(g289,g287)
    c: Weight(g290) = 1
    c: InternalAlignment(g291,g293)
    c: InternalAlignment(g292,g293)
    c: InternalAlignment(g294,g293)
    c: InternalAlignment(g295,g293)
    c: Weight(g296) = 1
    c: Equal(g296,g297)
    c: Equal(g296,g298)
    c: InternalAlignment(g296,g299)
    c: InternalAlignment(g297,g299)
    c: InternalAlignment(g298,g299)
    c: InternalAlignment(g300,g299)
    c: InternalAlignment(g301,g299)
    c: Equal(g302,g303)
    c: Equal(g302,g304)
    c: InternalAlignment(g302,g305)
    c: InternalAlignment(g303,g305)
    c: InternalAlignment(g304,g305)
    c: InternalAlignment(g306,g305)
    c: InternalAlignment(g307,g305)
    c: Block(g293)
    c: Block(g299)
    c: Block(g305)
    c: Block(g287)
    c: Coincident(g308,g287)
    c: Coincident(g308,g293)
    c: Horizontal(g308)
    c: Coincident(g309,g293)
    c: Coincident(g309,g299)
    c: Vertical(g309)
    c: Coincident(g310,g299)
    c: Coincident(g310,g305)
    c: Horizontal(g310)
    c: Coincident(g311,g305)
    c: Coincident(g311,g287)
    c: Weight(g312) = 1
    c: Equal(g312,g313)
    c: Equal(g312,g314)
    c: InternalAlignment(g312,g315)
    c: InternalAlignment(g313,g315)
    c: InternalAlignment(g314,g315)
    c: InternalAlignment(g316,g315)
    c: InternalAlignment(g317,g315)
    c: Weight(g318) = 1
    c: Equal(g318,g319)
    c: Equal(g318,g320)
    c: InternalAlignment(g318,g321)
    c: InternalAlignment(g319,g321)
    c: InternalAlignment(g320,g321)
    c: InternalAlignment(g322,g321)
    c: InternalAlignment(g323,g321)
    c: Weight(g324) = 1
    c: Equal(g324,g325)
    c: Equal(g324,g326)
    c: InternalAlignment(g324,g327)
    c: InternalAlignment(g325,g327)
    c: InternalAlignment(g326,g327)
    c: InternalAlignment(g328,g327)
    c: InternalAlignment(g329,g327)
    c: Block(g327)
    c: Block(g321)
    c: Block(g315)
    c: Coincident(g330,g327)
    c: Coincident(g330,g321)
    c: Horizontal(g330)
    c: Coincident(g331,g321)
    c: Coincident(g331,g315)
    c: Vertical(g331)
    c: Coincident(g332,g315)
    c: Coincident(g332,g327)
    c: InternalAlignment(g333,g334)
    c: InternalAlignment(g335,g334)
    c: InternalAlignment(g336,g334)
    c: Block(g334)
    c: Equal(g337,g338)
    c: Equal(g337,g339)
    c: InternalAlignment(g337,g340)
    c: InternalAlignment(g338,g340)
    c: InternalAlignment(g339,g340)
    c: InternalAlignment(g341,g340)
    c: InternalAlignment(g342,g340)
    c: Block(g340)
    c: Coincident(g343,g334)
    c: Horizontal(g343)
    c: Block(g343)
    c: Coincident(g344,g334)
    c: Coincident(g344,g260)
    c: Vertical(g344)
    c: Coincident(g345,g340)
    c: Coincident(g345,g254)
    c: Vertical(g345)
    c: Coincident(g347,g5)
    c: Coincident(g348,g5)
    c: Block(g346)
    c: Block(g5)
    c: Block(g348)
    c: Block(g347)
    c: Distance(g344) = 119.89
FEATURE [Sketcher::SketchObject] Sketch001
  FullyConstrained = true
  MapMode = 4
  Placement = pos=(0,0,0) rot=(0.57735,0.57735,0.57735;2.0944rad)
  Support = -> [Sketch]
  sketch-geometry (46):
    g0: BSplineCurve PolesCount=3 KnotsCount=2 Degree=2 IsPeriodic=0
    g1: ArcOfCircle CenterX=73.1223 CenterY=-32.291 CenterZ=0 NormalX=0 NormalY=0 NormalZ=1 AngleXU=0 Radius=13 StartAngle=5.92268 EndAngle=9.06428
    g2: ArcOfCircle CenterX=66.7816 CenterY=-49.1439 CenterZ=0 NormalX=0 NormalY=0 NormalZ=1 AngleXU=0 Radius=13 StartAngle=2.78068 EndAngle=5.92131
    g3: ArcOfCircle CenterX=55.9263 CenterY=-78.1807 CenterZ=0 NormalX=0 NormalY=0 NormalZ=1 AngleXU=0 Radius=13 StartAngle=5.92268 EndAngle=9.06428
    g4: ArcOfCircle CenterX=49.5884 CenterY=-95.0342 CenterZ=0 NormalX=0 NormalY=0 NormalZ=1 AngleXU=0 Radius=13 StartAngle=2.78068 EndAngle=5.92131
    g5: ArcOfCircle CenterX=38.7206 CenterY=-124.067 CenterZ=0 NormalX=0 NormalY=0 NormalZ=1 AngleXU=0 Radius=13 StartAngle=5.92268 EndAngle=9.06428
    g6: ArcOfCircle CenterX=32.3875 CenterY=-140.92 CenterZ=0 NormalX=0 NormalY=0 NormalZ=1 AngleXU=0 Radius=13 StartAngle=2.78068 EndAngle=5.92131
    g7: ArcOfCircle CenterX=21.4715 CenterY=-169.934 CenterZ=0 NormalX=0 NormalY=0 NormalZ=1 AngleXU=0 Radius=13 StartAngle=5.92268 EndAngle=9.06428
    g8: ArcOfCircle CenterX=15.1336 CenterY=-186.787 CenterZ=0 NormalX=0 NormalY=0 NormalZ=1 AngleXU=0 Radius=13 StartAngle=2.78068 EndAngle=5.92131
    g9-g12: Circle x4 (B-spline internal-alignment scaffolding for g13; pole/knot coordinates omitted)
    g13: BSplineCurve PolesCount=4 KnotsCount=2 Degree=3 IsPeriodic=0
    g14: GeomPoint X=28.8094 Y=-19.0875 Z=0
    g15: GeomPoint X=47.0443 Y=-50.4712 Z=0
    g16: Circle CenterX=53.5586 CenterY=-23.2695 CenterZ=0 NormalX=0 NormalY=0 NormalZ=1 AngleXU=0 Radius=3.24518
    g17: Circle CenterX=-195.441 CenterY=-127.082 CenterZ=0 NormalX=0 NormalY=0 NormalZ=1 AngleXU=0 Radius=1
    g18: Circle CenterX=-8.24091 CenterY=-197.481 CenterZ=0 NormalX=0 NormalY=0 NormalZ=1 AngleXU=0 Radius=1
    g19: Circle CenterX=12.8789 CenterY=-141.321 CenterZ=0 NormalX=0 NormalY=0 NormalZ=1 AngleXU=0 Radius=1
    g20: BSplineCurve PolesCount=3 KnotsCount=2 Degree=2 IsPeriodic=0
    g21: GeomPoint X=-195.441 Y=-127.082 Z=0
    g22: GeomPoint X=12.8789 Y=-141.321 Z=0
    g23: Circle CenterX=-12.8016 CenterY=-179.036 CenterZ=0 NormalX=0 NormalY=0 NormalZ=1 AngleXU=0 Radius=10.5072
    g24: Circle CenterX=0.933922 CenterY=-166.43 CenterZ=0 NormalX=0 NormalY=0 NormalZ=1 AngleXU=0 Radius=3.26661
    g25: Circle CenterX=-33.5518 CenterY=-176.44 CenterZ=0 NormalX=0 NormalY=0 NormalZ=1 AngleXU=0 Radius=5.64388
    g26: Circle CenterX=-47.2366 CenterY=-173.859 CenterZ=0 NormalX=0 NormalY=0 NormalZ=1 AngleXU=0 Radius=3.01653
    g27: Circle CenterX=-56.2595 CenterY=-171.456 CenterZ=0 NormalX=0 NormalY=0 NormalZ=1 AngleXU=0 Radius=2.12826
    g28: ArcOfCircle CenterX=51.2151 CenterY=-198.473 CenterZ=0 NormalX=0 NormalY=0 NormalZ=1 AngleXU=0 Radius=20 StartAngle=2.78189 EndAngle=4.35269
    g29: LineSegment StartX=32.4951 StartY=-191.433 StartZ=0 EndX=94.6578 EndY=-26.1352 EndZ=0
    g30: LineSegment StartX=43.1192 StartY=-220.001 StartZ=0 EndX=-196.497 EndY=-129.89 EndZ=0
    g31: LineSegment StartX=43.1192 StartY=-220.001 StartZ=0 EndX=44.1752 EndY=-217.193 EndZ=0
    g32: LineSegment StartX=117.223 StartY=-19.0875 StartZ=0 EndX=117.223 EndY=-16.0875 EndZ=0
    g33: LineSegment StartX=117.223 StartY=-16.0875 StartZ=0 EndX=17.2232 EndY=-16.0875 EndZ=0
    g34: LineSegment StartX=17.2232 StartY=-16.0875 StartZ=0 EndX=17.2232 EndY=-19.0875 EndZ=0
    g35: LineSegment StartX=28.8094 StartY=-19.0875 StartZ=0 EndX=17.2232 EndY=-19.0875 EndZ=0
    g36: LineSegment StartX=47.0443 StartY=-50.4712 StartZ=0 EndX=12.8789 EndY=-141.321 EndZ=0
    g37: LineSegment StartX=-195.441 StartY=-127.082 StartZ=0 EndX=-196.497 EndY=-129.89 EndZ=0
    g38: LineSegment StartX=85.2866 StartY=-36.8766 StartZ=0 EndX=78.9396 EndY=-53.7463 EndZ=0
    g39: LineSegment StartX=60.9579 StartY=-27.7053 StartZ=0 EndX=54.6191 EndY=-44.5532 EndZ=0
    g40: LineSegment StartX=68.0907 StartY=-82.7664 StartZ=0 EndX=61.7465 EndY=-99.6365 EndZ=0
    g41: LineSegment StartX=43.7619 StartY=-73.595 StartZ=0 EndX=37.426 EndY=-90.4435 EndZ=0
    g42: LineSegment StartX=50.885 StartY=-128.652 StartZ=0 EndX=44.5456 EndY=-145.522 EndZ=0
    g43: LineSegment StartX=26.5562 StartY=-119.481 StartZ=0 EndX=20.2251 EndY=-136.329 EndZ=0
    g44: LineSegment StartX=9.3071 StartY=-165.349 StartZ=0 EndX=2.97115 EndY=-182.197 EndZ=0
    g45: LineSegment StartX=33.6358 StartY=-174.52 StartZ=0 EndX=27.2917 EndY=-191.39 EndZ=0
  constraints (71):
    c: Block(g0)
    c: Block(g1)
    c: Block(g2)
    c: Block(g4)
    c: Block(g3)
    c: Block(g6)
    c: Block(g5)
    c: Block(g8)
    c: Block(g7)
    c: Weight(g9) = 1
    c: Equal(g9,g10)
    c: Equal(g9,g11)
    c: Equal(g9,g12)
    c: InternalAlignment(g9-g12 -> g13) x4
    c: InternalAlignment(g14,g13)
    c: InternalAlignment(g15,g13)
    c: Block(g16)
    c: Weight(g17) = 1
    c: Equal(g17,g18)
    c: Equal(g17,g19)
    c: InternalAlignment(g17,g20)
    c: InternalAlignment(g18,g20)
    c: InternalAlignment(g19,g20)
    c: InternalAlignment(g21,g20)
    c: InternalAlignment(g22,g20)
    c: Block(g20)
    c: Block(g23)
    c: Block(g24)
    c: Block(g25)
    c: Block(g26)
    c: Block(g27)
    c: Block(g28)
    c: Coincident(g29,g28)
    c: Coincident(g29,g0)
    c: Block(g13)
    c: Coincident(g31,g30)
    c: Coincident(g31,g28)
    c: Block(g31)
    c: Coincident(g32,g0)
    c: Vertical(g32)
    c: Coincident(g33,g32)
    c: Horizontal(g33)
    c: Coincident(g34,g33)
    c: Vertical(g34)
    c: Block(g33)
    c: Coincident(g35,g13)
    c: Coincident(g35,g34)
    c: Horizontal(g35)
    c: Coincident(g36,g13)
    c: Coincident(g36,g20)
    c: Coincident(g37,g20)
    c: Coincident(g37,g30)
    c: Block(g30)
    c: Coincident(g38,g1)
    c: Coincident(g38,g2)
    c: Coincident(g39,g1)
    c: Coincident(g39,g2)
    c: Coincident(g40,g3)
    c: Coincident(g40,g4)
    c: Coincident(g41,g3)
    c: Coincident(g41,g4)
    c: Coincident(g42,g5)
    c: Coincident(g42,g6)
    c: Coincident(g43,g5)
    c: Coincident(g43,g6)
    c: Coincident(g44,g7)
    c: Coincident(g44,g8)
    c: Coincident(g45,g7)
    c: Coincident(g45,g8)
    c: Distance(g30) = 256
    c: Distance(g33) = 100
FEATURE [Part::Extrusion] Extrude002
  Base = -> Sketch001
  Dir = (1,0,0)
  DirMode = 2
  FaceMakerClass = Part::FaceMakerBullseye
  LengthFwd = 8
  LengthRev = 0
  Solid = true
  Symmetric = false
FEATURE [Sketcher::SketchObject] Sketch002
  FullyConstrained = true
  sketch-geometry (20):
    g0: LineSegment StartX=-2.77179 StartY=-200.304 StartZ=0 EndX=5.22821 EndY=-200.304 EndZ=0
    g1: LineSegment StartX=5.22821 StartY=-200.304 StartZ=0 EndX=5.22821 EndY=-197.304 EndZ=0
    g2: LineSegment StartX=-2.77179 StartY=-200.304 StartZ=0 EndX=-2.77179 EndY=-197.304 EndZ=0
    g3: LineSegment StartX=5.22821 StartY=-197.304 StartZ=0 EndX=8.22821 EndY=-197.304 EndZ=0
    g4: LineSegment StartX=-2.77179 StartY=-197.304 StartZ=0 EndX=-5.77179 EndY=-197.304 EndZ=0
    g5: LineSegment StartX=19.2282 StartY=-203.304 StartZ=0 EndX=19.2282 EndY=-206.304 EndZ=0
    g6: LineSegment StartX=-16.7718 StartY=-203.304 StartZ=0 EndX=-16.7718 EndY=-206.304 EndZ=0
    g7: LineSegment StartX=-16.7718 StartY=-206.304 StartZ=0 EndX=19.2282 EndY=-206.304 EndZ=0
    g8: Circle CenterX=-16.7718 CenterY=-203.304 CenterZ=0 NormalX=0 NormalY=0 NormalZ=1 AngleXU=0 Radius=1
    g9: Circle CenterX=-5.77179 CenterY=-203.304 CenterZ=0 NormalX=0 NormalY=0 NormalZ=1 AngleXU=0 Radius=1
    g10: Circle CenterX=-5.77179 CenterY=-197.304 CenterZ=0 NormalX=0 NormalY=0 NormalZ=1 AngleXU=0 Radius=1
    g11: BSplineCurve PolesCount=3 KnotsCount=2 Degree=2 IsPeriodic=0
    g12: GeomPoint X=-16.7718 Y=-203.304 Z=0
    g13: GeomPoint X=-5.77179 Y=-197.304 Z=0
    g14: Circle CenterX=19.2282 CenterY=-203.304 CenterZ=0 NormalX=0 NormalY=0 NormalZ=1 AngleXU=0 Radius=1
    g15: Circle CenterX=8.22821 CenterY=-203.304 CenterZ=0 NormalX=0 NormalY=0 NormalZ=1 AngleXU=0 Radius=1
    g16: Circle CenterX=8.22821 CenterY=-197.304 CenterZ=0 NormalX=0 NormalY=0 NormalZ=1 AngleXU=0 Radius=1
    g17: BSplineCurve PolesCount=3 KnotsCount=2 Degree=2 IsPeriodic=0
    g18: GeomPoint X=19.2282 Y=-203.304 Z=0
    g19: GeomPoint X=8.22821 Y=-197.304 Z=0
  constraints (41):
    c: Horizontal(g0)
    c: Distance(g0) = 8
    c: Coincident(g1,g0)
    c: Vertical(g1)
    c: Distance(g1) = 3
    c: Coincident(g2,g0)
    c: Vertical(g2)
    c: Distance(g2) = 3
    c: Coincident(g3,g1)
    c: Horizontal(g3)
    c: Distance(g3) = 3
    c: Coincident(g4,g2)
    c: Horizontal(g4)
    c: Distance(g4) = 3
    c: Vertical(g5)
    c: Vertical(g6)
    c: Coincident(g7,g6)
    c: Coincident(g7,g5)
    c: Weight(g8) = 1
    c: Equal(g8,g9)
    c: Equal(g8,g10)
    c: Coincident(g11,g4)
    c: InternalAlignment(g8,g11)
    c: InternalAlignment(g9,g11)
    c: InternalAlignment(g10,g11)
    c: InternalAlignment(g12,g11)
    c: InternalAlignment(g13,g11)
    c: Coincident(g17,g5)
    c: Weight(g14) = 1
    c: Equal(g14,g15)
    c: Equal(g14,g16)
    c: Coincident(g17,g3)
    c: InternalAlignment(g14,g17)
    c: InternalAlignment(g15,g17)
    c: InternalAlignment(g16,g17)
    c: InternalAlignment(g18,g17)
    c: InternalAlignment(g19,g17)
    c: Block(g7)
    c: Block(g17)
    c: Block(g11)
    c: Block(g6)
FEATURE [Part::Extrusion] Extrude003
  Base = -> Sketch002
  Dir = (0,0,1)
  DirMode = 2
  FaceMakerClass = Part::FaceMakerBullseye
  LengthFwd = 260
  LengthRev = 0
  Solid = true
  Symmetric = false
FEATURE [Part::Extrusion] Extrude
  Base = -> Sketch
  Dir = (0,0,1)
  DirMode = 2
  FaceMakerClass = Part::FaceMakerBullseye
  LengthFwd = 14
  LengthRev = 0
  Solid = true
  Symmetric = false
FEATURE [Sketcher::SketchObject] Sketch003
  FullyConstrained = false
  sketch-geometry (381):
    g0: LineSegment StartX=-10.9272 StartY=-82.7794 StartZ=0 EndX=46.0728 EndY=-51.4823 EndZ=0
    g1: LineSegment StartX=-10.9272 StartY=76.4095 StartZ=0 EndX=-10.9272 EndY=-82.7794 EndZ=0
    g2: LineSegment StartX=46.0728 StartY=76.4095 StartZ=0 EndX=46.0728 EndY=-51.4823 EndZ=0
    g3: LineSegment StartX=-42.9272 StartY=136.221 StartZ=0 EndX=-42.9272 EndY=-103.779 EndZ=0
    g4: LineSegment StartX=407.073 StartY=136.221 StartZ=0 EndX=407.073 EndY=-103.779 EndZ=0
    g5: ArcOfCircle CenterX=-26.9272 CenterY=-83.7794 CenterZ=0 NormalX=0 NormalY=0 NormalZ=1 AngleXU=0 Radius=8 StartAngle=3.14159 EndAngle=6.28319
    g6: ArcOfCircle CenterX=391.073 CenterY=-83.7794 CenterZ=0 NormalX=0 NormalY=0 NormalZ=1 AngleXU=0 Radius=8 StartAngle=3.14159 EndAngle=6.28319
    g7: Circle CenterX=175.022 CenterY=27.0628 CenterZ=0 NormalX=0 NormalY=0 NormalZ=1 AngleXU=0 Radius=1
    g8: Circle CenterX=179.022 CenterY=24.8665 CenterZ=0 NormalX=0 NormalY=0 NormalZ=1 AngleXU=0 Radius=1
    g9: Circle CenterX=179.022 CenterY=27.0628 CenterZ=0 NormalX=0 NormalY=0 NormalZ=1 AngleXU=0 Radius=1
    g10: BSplineCurve PolesCount=3 KnotsCount=2 Degree=2 IsPeriodic=0
    g11: GeomPoint X=175.022 Y=27.0628 Z=0
    g12: GeomPoint X=179.022 Y=27.0628 Z=0
    g13: Circle CenterX=189.124 CenterY=27.0628 CenterZ=0 NormalX=0 NormalY=0 NormalZ=1 AngleXU=0 Radius=1
    g14: Circle CenterX=185.124 CenterY=24.8665 CenterZ=0 NormalX=0 NormalY=0 NormalZ=1 AngleXU=0 Radius=1
    g15: Circle CenterX=185.124 CenterY=27.0628 CenterZ=0 NormalX=0 NormalY=0 NormalZ=1 AngleXU=0 Radius=1
    g16: BSplineCurve PolesCount=3 KnotsCount=2 Degree=2 IsPeriodic=0
    g17: GeomPoint X=189.124 Y=27.0628 Z=0
    g18: GeomPoint X=185.124 Y=27.0628 Z=0
    g19: Circle CenterX=175.022 CenterY=5.37834 CenterZ=0 NormalX=0 NormalY=0 NormalZ=1 AngleXU=0 Radius=1
    g20: Circle CenterX=179.022 CenterY=7.57463 CenterZ=0 NormalX=0 NormalY=0 NormalZ=1 AngleXU=0 Radius=1
    g21: Circle CenterX=179.022 CenterY=5.34704 CenterZ=0 NormalX=0 NormalY=0 NormalZ=1 AngleXU=0 Radius=1
    g22: BSplineCurve PolesCount=3 KnotsCount=2 Degree=2 IsPeriodic=0
    g23: GeomPoint X=175.022 Y=5.37834 Z=0
    g24: GeomPoint X=179.022 Y=5.34704 Z=0
    g25: Circle CenterX=189.124 CenterY=5.37834 CenterZ=0 NormalX=0 NormalY=0 NormalZ=1 AngleXU=0 Radius=1
    g26: Circle CenterX=185.124 CenterY=7.57463 CenterZ=0 NormalX=0 NormalY=0 NormalZ=1 AngleXU=0 Radius=1
    g27: Circle CenterX=185.124 CenterY=5.34704 CenterZ=0 NormalX=0 NormalY=0 NormalZ=1 AngleXU=0 Radius=1
    g28: BSplineCurve PolesCount=3 KnotsCount=2 Degree=2 IsPeriodic=0
    g29: GeomPoint X=189.124 Y=5.37834 Z=0
    g30: GeomPoint X=185.124 Y=5.34704 Z=0
    g31: Circle CenterX=165.871 CenterY=18.1458 CenterZ=0 NormalX=0 NormalY=0 NormalZ=1 AngleXU=0 Radius=1
    g32: Circle CenterX=169.377 CenterY=16.2206 CenterZ=0 NormalX=0 NormalY=0 NormalZ=1 AngleXU=0 Radius=1
    g33: Circle CenterX=165.871 CenterY=14.2954 CenterZ=0 NormalX=0 NormalY=0 NormalZ=1 AngleXU=0 Radius=1
    g34: BSplineCurve PolesCount=3 KnotsCount=2 Degree=2 IsPeriodic=0
    g35: GeomPoint X=165.871 Y=18.1458 Z=0
    g36: GeomPoint X=165.871 Y=14.2954 Z=0
    g37: Circle CenterX=198.275 CenterY=18.1458 CenterZ=0 NormalX=0 NormalY=0 NormalZ=1 AngleXU=0 Radius=1
    g38: Circle CenterX=194.768 CenterY=16.2206 CenterZ=0 NormalX=0 NormalY=0 NormalZ=1 AngleXU=0 Radius=1
    g39: Circle CenterX=198.275 CenterY=14.2954 CenterZ=0 NormalX=0 NormalY=0 NormalZ=1 AngleXU=0 Radius=1
    g40: BSplineCurve PolesCount=3 KnotsCount=2 Degree=2 IsPeriodic=0
    g41: GeomPoint X=198.275 Y=18.1458 Z=0
    g42: GeomPoint X=198.275 Y=14.2954 Z=0
    g43: LineSegment StartX=407.073 StartY=-103.779 StartZ=0 EndX=-42.9272 EndY=-103.779 EndZ=0
    g44: LineSegment StartX=407.073 StartY=136.221 StartZ=0 EndX=-42.9272 EndY=136.221 EndZ=0
    g45: LineSegment StartX=46.0728 StartY=76.4095 StartZ=0 EndX=-10.9272 EndY=76.4095 EndZ=0
    g46: Circle CenterX=125.607 CenterY=54.1951 CenterZ=0 NormalX=0 NormalY=0 NormalZ=1 AngleXU=0 Radius=1
    g47: Circle CenterX=139.632 CenterY=46.4944 CenterZ=0 NormalX=0 NormalY=0 NormalZ=1 AngleXU=0 Radius=1
    g48: Circle CenterX=127.326 CenterY=56.7187 CenterZ=0 NormalX=0 NormalY=0 NormalZ=1 AngleXU=0 Radius=1
    g49: BSplineCurve PolesCount=3 KnotsCount=2 Degree=2 IsPeriodic=0
    g50: GeomPoint X=125.607 Y=54.1951 Z=0
    g51: GeomPoint X=127.326 Y=56.7187 Z=0
    g52: Circle CenterX=236.821 CenterY=56.7187 CenterZ=0 NormalX=0 NormalY=0 NormalZ=1 AngleXU=0 Radius=1
    g53: Circle CenterX=224.513 CenterY=46.4944 CenterZ=0 NormalX=0 NormalY=0 NormalZ=1 AngleXU=0 Radius=1
    g54: Circle CenterX=238.538 CenterY=54.1951 CenterZ=0 NormalX=0 NormalY=0 NormalZ=1 AngleXU=0 Radius=1
    g55: BSplineCurve PolesCount=3 KnotsCount=2 Degree=2 IsPeriodic=0
    g56: GeomPoint X=236.821 Y=56.7187 Z=0
    g57: GeomPoint X=238.538 Y=54.1951 Z=0
    g58: Circle CenterX=238.538 CenterY=-21.7539 CenterZ=0 NormalX=0 NormalY=0 NormalZ=1 AngleXU=0 Radius=1
    g59: Circle CenterX=224.513 CenterY=-14.0532 CenterZ=0 NormalX=0 NormalY=0 NormalZ=1 AngleXU=0 Radius=1
    g60: Circle CenterX=236.821 CenterY=-24.2775 CenterZ=0 NormalX=0 NormalY=0 NormalZ=1 AngleXU=0 Radius=1
    g61: BSplineCurve PolesCount=3 KnotsCount=2 Degree=2 IsPeriodic=0
    g62: GeomPoint X=238.538 Y=-21.7539 Z=0
    g63: GeomPoint X=236.821 Y=-24.2775 Z=0
    g64: Circle CenterX=125.607 CenterY=-21.7539 CenterZ=0 NormalX=0 NormalY=0 NormalZ=1 AngleXU=0 Radius=1
    g65: Circle CenterX=139.632 CenterY=-14.0532 CenterZ=0 NormalX=0 NormalY=0 NormalZ=1 AngleXU=0 Radius=1
    g66: Circle CenterX=127.325 CenterY=-24.2775 CenterZ=0 NormalX=0 NormalY=0 NormalZ=1 AngleXU=0 Radius=1
    g67: BSplineCurve PolesCount=3 KnotsCount=2 Degree=2 IsPeriodic=0
    g68: GeomPoint X=125.607 Y=-21.7539 Z=0
    g69: GeomPoint X=127.325 Y=-24.2775 Z=0
    g70: Circle CenterX=302.996 CenterY=111.695 CenterZ=0 NormalX=0 NormalY=0 NormalZ=1 AngleXU=0 Radius=1
    g71: Circle CenterX=306.073 CenterY=114.251 CenterZ=0 NormalX=0 NormalY=0 NormalZ=1 AngleXU=0 Radius=1
    g72: Circle CenterX=306.073 CenterY=110.251 CenterZ=0 NormalX=0 NormalY=0 NormalZ=1 AngleXU=0 Radius=1
    g73: BSplineCurve PolesCount=3 KnotsCount=2 Degree=2 IsPeriodic=0
    g74: GeomPoint X=302.996 Y=111.695 Z=0
    g75: GeomPoint X=306.073 Y=110.251 Z=0
    g76: Circle CenterX=306.073 CenterY=95.2763 CenterZ=0 NormalX=0 NormalY=0 NormalZ=1 AngleXU=0 Radius=1
    g77: Circle CenterX=306.073 CenterY=91.2763 CenterZ=0 NormalX=0 NormalY=0 NormalZ=1 AngleXU=0 Radius=1
    g78: Circle CenterX=302.567 CenterY=89.3511 CenterZ=0 NormalX=0 NormalY=0 NormalZ=1 AngleXU=0 Radius=1
    g79: BSplineCurve PolesCount=3 KnotsCount=2 Degree=2 IsPeriodic=0
    g80: GeomPoint X=306.073 Y=95.2763 Z=0
    g81: GeomPoint X=302.567 Y=89.3511 Z=0
    g82: LineSegment StartX=306.073 StartY=110.251 StartZ=0 EndX=306.073 EndY=95.2763 EndZ=0
    g83: LineSegment StartX=302.996 StartY=111.695 StartZ=0 EndX=236.821 EndY=56.7187 EndZ=0
    g84: LineSegment StartX=238.538 StartY=54.1951 StartZ=0 EndX=302.567 EndY=89.3511 EndZ=0
    g85: Circle CenterX=61.1496 CenterY=111.695 CenterZ=0 NormalX=0 NormalY=0 NormalZ=1 AngleXU=0 Radius=1
    g86: Circle CenterX=58.0728 CenterY=114.251 CenterZ=0 NormalX=0 NormalY=0 NormalZ=1 AngleXU=0 Radius=1
    g87: Circle CenterX=58.0728 CenterY=110.251 CenterZ=0 NormalX=0 NormalY=0 NormalZ=1 AngleXU=0 Radius=1
    g88: BSplineCurve PolesCount=3 KnotsCount=2 Degree=2 IsPeriodic=0
    g89: GeomPoint X=61.1496 Y=111.695 Z=0
    g90: GeomPoint X=58.0728 Y=110.251 Z=0
    g91: Circle CenterX=61.5791 CenterY=89.3511 CenterZ=0 NormalX=0 NormalY=0 NormalZ=1 AngleXU=0 Radius=1
    g92: Circle CenterX=58.0728 CenterY=91.2763 CenterZ=0 NormalX=0 NormalY=0 NormalZ=1 AngleXU=0 Radius=1
    g93: Circle CenterX=58.0728 CenterY=95.2763 CenterZ=0 NormalX=0 NormalY=0 NormalZ=1 AngleXU=0 Radius=1
    g94: BSplineCurve PolesCount=3 KnotsCount=2 Degree=2 IsPeriodic=0
    g95: GeomPoint X=61.5791 Y=89.3511 Z=0
    g96: GeomPoint X=58.0728 Y=95.2763 Z=0
    g97: LineSegment StartX=58.0728 StartY=110.251 StartZ=0 EndX=58.0728 EndY=95.2763 EndZ=0
    g98: LineSegment StartX=61.1496 StartY=111.695 StartZ=0 EndX=127.326 EndY=56.7187 EndZ=0
    g99: LineSegment StartX=125.607 StartY=54.1951 StartZ=0 EndX=61.5791 EndY=89.3511 EndZ=0
    g100: Circle CenterX=61.5791 CenterY=-56.9099 CenterZ=0 NormalX=0 NormalY=0 NormalZ=1 AngleXU=0 Radius=1
    g101: Circle CenterX=58.0728 CenterY=-58.8351 CenterZ=0 NormalX=0 NormalY=0 NormalZ=1 AngleXU=0 Radius=1
    g102: Circle CenterX=58.0728 CenterY=-62.8351 CenterZ=0 NormalX=0 NormalY=0 NormalZ=1 AngleXU=0 Radius=1
    g103: BSplineCurve PolesCount=3 KnotsCount=2 Degree=2 IsPeriodic=0
    g104: GeomPoint X=61.5791 Y=-56.9099 Z=0
    g105: GeomPoint X=58.0728 Y=-62.8351 Z=0
    g106: Circle CenterX=58.0728 CenterY=-77.8102 CenterZ=0 NormalX=0 NormalY=0 NormalZ=1 AngleXU=0 Radius=1
    g107: Circle CenterX=58.0728 CenterY=-81.8102 CenterZ=0 NormalX=0 NormalY=0 NormalZ=1 AngleXU=0 Radius=1
    g108: Circle CenterX=61.1496 CenterY=-79.2541 CenterZ=0 NormalX=0 NormalY=0 NormalZ=1 AngleXU=0 Radius=1
    g109: BSplineCurve PolesCount=3 KnotsCount=2 Degree=2 IsPeriodic=0
    g110: GeomPoint X=58.0728 Y=-77.8102 Z=0
    g111: GeomPoint X=61.1496 Y=-79.2541 Z=0
    g112: LineSegment StartX=58.0728 StartY=-62.8351 StartZ=0 EndX=58.0728 EndY=-77.8102 EndZ=0
    g113: LineSegment StartX=61.1496 StartY=-79.2541 StartZ=0 EndX=127.325 EndY=-24.2775 EndZ=0
    g114: LineSegment StartX=125.607 StartY=-21.7539 StartZ=0 EndX=61.5791 EndY=-56.9099 EndZ=0
    g115: Circle CenterX=302.567 CenterY=-56.9099 CenterZ=0 NormalX=0 NormalY=0 NormalZ=1 AngleXU=0 Radius=1
    g116: Circle CenterX=306.073 CenterY=-58.8351 CenterZ=0 NormalX=0 NormalY=0 NormalZ=1 AngleXU=0 Radius=1
    g117: Circle CenterX=306.073 CenterY=-62.8351 CenterZ=0 NormalX=0 NormalY=0 NormalZ=1 AngleXU=0 Radius=1
    g118: BSplineCurve PolesCount=3 KnotsCount=2 Degree=2 IsPeriodic=0
    g119: GeomPoint X=302.567 Y=-56.9099 Z=0
    g120: GeomPoint X=306.073 Y=-62.8351 Z=0
    g121: Circle CenterX=302.996 CenterY=-79.2541 CenterZ=0 NormalX=0 NormalY=0 NormalZ=1 AngleXU=0 Radius=1
    g122: Circle CenterX=306.073 CenterY=-81.8102 CenterZ=0 NormalX=0 NormalY=0 NormalZ=1 AngleXU=0 Radius=1
    g123: Circle CenterX=306.073 CenterY=-77.8102 CenterZ=0 NormalX=0 NormalY=0 NormalZ=1 AngleXU=0 Radius=1
    g124: BSplineCurve PolesCount=3 KnotsCount=2 Degree=2 IsPeriodic=0
    g125: GeomPoint X=302.996 Y=-79.2541 Z=0
    g126: GeomPoint X=306.073 Y=-77.8102 Z=0
    g127: LineSegment StartX=306.073 StartY=-62.8351 StartZ=0 EndX=306.073 EndY=-77.8102 EndZ=0
    g128: LineSegment StartX=302.996 StartY=-79.2541 StartZ=0 EndX=236.821 EndY=-24.2775 EndZ=0
    g129: LineSegment StartX=238.538 StartY=-21.7539 StartZ=0 EndX=302.567 EndY=-56.9099 EndZ=0
    g130: Circle CenterX=61.6457 CenterY=-88.8112 CenterZ=0 NormalX=0 NormalY=0 NormalZ=1 AngleXU=0 Radius=1
    g131: Circle CenterX=58.0728 CenterY=-91.7794 CenterZ=0 NormalX=0 NormalY=0 NormalZ=1 AngleXU=0 Radius=1
    g132: Circle CenterX=63.9135 CenterY=-91.7794 CenterZ=0 NormalX=0 NormalY=0 NormalZ=1 AngleXU=0 Radius=1
    g133: BSplineCurve PolesCount=3 KnotsCount=2 Degree=2 IsPeriodic=0
    g134: GeomPoint X=61.6457 Y=-88.8112 Z=0
    g135: GeomPoint X=63.9135 Y=-91.7794 Z=0
    g136: Circle CenterX=179.022 CenterY=-85.8163 CenterZ=0 NormalX=0 NormalY=0 NormalZ=1 AngleXU=0 Radius=1
    g137: Circle CenterX=179.022 CenterY=-91.7794 CenterZ=0 NormalX=0 NormalY=0 NormalZ=1 AngleXU=0 Radius=1
    g138: Circle CenterX=171.895 CenterY=-91.7794 CenterZ=0 NormalX=0 NormalY=0 NormalZ=1 AngleXU=0 Radius=1
    g139: BSplineCurve PolesCount=3 KnotsCount=2 Degree=2 IsPeriodic=0
    g140: GeomPoint X=179.022 Y=-85.8163 Z=0
    g141: GeomPoint X=171.895 Y=-91.7794 Z=0
    g142: Circle CenterX=185.124 CenterY=-86.2028 CenterZ=0 NormalX=0 NormalY=0 NormalZ=1 AngleXU=0 Radius=1
    g143: Circle CenterX=185.124 CenterY=-91.7794 CenterZ=0 NormalX=0 NormalY=0 NormalZ=1 AngleXU=0 Radius=1
    g144: Circle CenterX=191.747 CenterY=-91.7794 CenterZ=0 NormalX=0 NormalY=0 NormalZ=1 AngleXU=0 Radius=1
    g145: BSplineCurve PolesCount=3 KnotsCount=2 Degree=2 IsPeriodic=0
    g146: GeomPoint X=185.124 Y=-86.2028 Z=0
    g147: GeomPoint X=191.747 Y=-91.7794 Z=0
    g148: Circle CenterX=299.888 CenterY=-86.6413 CenterZ=0 NormalX=0 NormalY=0 NormalZ=1 AngleXU=0 Radius=1
    g149: Circle CenterX=306.073 CenterY=-91.7794 CenterZ=0 NormalX=0 NormalY=0 NormalZ=1 AngleXU=0 Radius=1
    g150: Circle CenterX=298.776 CenterY=-91.7794 CenterZ=0 NormalX=0 NormalY=0 NormalZ=1 AngleXU=0 Radius=1
    g151: BSplineCurve PolesCount=3 KnotsCount=2 Degree=2 IsPeriodic=0
    g152: GeomPoint X=299.888 Y=-86.6413 Z=0
    g153: GeomPoint X=298.776 Y=-91.7794 Z=0
    g154: LineSegment StartX=189.124 StartY=5.37834 StartZ=0 EndX=299.888 EndY=-86.6413 EndZ=0
    g155: LineSegment StartX=298.776 StartY=-91.7794 StartZ=0 EndX=191.747 EndY=-91.7794 EndZ=0
    g156: LineSegment StartX=185.124 StartY=-86.2028 StartZ=0 EndX=185.124 EndY=5.34704 EndZ=0
    g157: LineSegment StartX=179.022 StartY=5.34704 StartZ=0 EndX=179.022 EndY=-85.8163 EndZ=0
    g158: LineSegment StartX=171.895 StartY=-91.7794 StartZ=0 EndX=63.9135 EndY=-91.7794 EndZ=0
    g159: LineSegment StartX=61.6457 StartY=-88.8112 StartZ=0 EndX=175.022 EndY=5.37834 EndZ=0
    g160: Circle CenterX=302.073 CenterY=124.221 CenterZ=0 NormalX=0 NormalY=0 NormalZ=1 AngleXU=0 Radius=1
    g161: Circle CenterX=306.073 CenterY=124.221 CenterZ=0 NormalX=0 NormalY=0 NormalZ=1 AngleXU=0 Radius=1
    g162: Circle CenterX=302.996 CenterY=121.665 CenterZ=0 NormalX=0 NormalY=0 NormalZ=1 AngleXU=0 Radius=1
    g163: BSplineCurve PolesCount=3 KnotsCount=2 Degree=2 IsPeriodic=0
    g164: GeomPoint X=302.073 Y=124.221 Z=0
    g165: GeomPoint X=302.996 Y=121.665 Z=0
    g166: Circle CenterX=189.124 CenterY=124.221 CenterZ=0 NormalX=0 NormalY=0 NormalZ=1 AngleXU=0 Radius=1
    g167: Circle CenterX=185.124 CenterY=124.221 CenterZ=0 NormalX=0 NormalY=0 NormalZ=1 AngleXU=0 Radius=1
    g168: Circle CenterX=185.124 CenterY=120.221 CenterZ=0 NormalX=0 NormalY=0 NormalZ=1 AngleXU=0 Radius=1
    g169: BSplineCurve PolesCount=3 KnotsCount=2 Degree=2 IsPeriodic=0
    g170: GeomPoint X=189.124 Y=124.221 Z=0
    g171: GeomPoint X=185.124 Y=120.221 Z=0
    g172: Circle CenterX=175.022 CenterY=124.221 CenterZ=0 NormalX=0 NormalY=0 NormalZ=1 AngleXU=0 Radius=1
    g173: Circle CenterX=179.022 CenterY=124.221 CenterZ=0 NormalX=0 NormalY=0 NormalZ=1 AngleXU=0 Radius=1
    g174: Circle CenterX=179.022 CenterY=120.221 CenterZ=0 NormalX=0 NormalY=0 NormalZ=1 AngleXU=0 Radius=1
    g175: BSplineCurve PolesCount=3 KnotsCount=2 Degree=2 IsPeriodic=0
    g176: GeomPoint X=175.022 Y=124.221 Z=0
    g177: GeomPoint X=179.022 Y=120.221 Z=0
    g178: Circle CenterX=62.0728 CenterY=124.221 CenterZ=0 NormalX=0 NormalY=0 NormalZ=1 AngleXU=0 Radius=1
    g179: Circle CenterX=58.0728 CenterY=124.221 CenterZ=0 NormalX=0 NormalY=0 NormalZ=1 AngleXU=0 Radius=1
    g180: Circle CenterX=61.1496 CenterY=121.665 CenterZ=0 NormalX=0 NormalY=0 NormalZ=1 AngleXU=0 Radius=1
    g181: BSplineCurve PolesCount=3 KnotsCount=2 Degree=2 IsPeriodic=0
    g182: GeomPoint X=62.0728 Y=124.221 Z=0
    g183: GeomPoint X=61.1496 Y=121.665 Z=0
    g184: LineSegment StartX=62.0728 StartY=124.221 StartZ=0 EndX=175.022 EndY=124.221 EndZ=0
    g185: LineSegment StartX=179.022 StartY=120.221 StartZ=0 EndX=179.022 EndY=27.0628 EndZ=0
    g186: LineSegment StartX=185.124 StartY=27.0628 StartZ=0 EndX=185.124 EndY=120.221 EndZ=0
    g187: LineSegment StartX=189.124 StartY=124.221 StartZ=0 EndX=302.073 EndY=124.221 EndZ=0
    g188: LineSegment StartX=302.996 StartY=121.665 StartZ=0 EndX=189.124 EndY=27.0628 EndZ=0
    g189: LineSegment StartX=175.022 StartY=27.0628 StartZ=0 EndX=61.1496 EndY=121.665 EndZ=0
    g190: Circle CenterX=61.5791 CenterY=75.4095 CenterZ=0 NormalX=0 NormalY=0 NormalZ=1 AngleXU=0 Radius=1
    g191: Circle CenterX=58.0728 CenterY=77.3346 CenterZ=0 NormalX=0 NormalY=0 NormalZ=1 AngleXU=0 Radius=1
    g192: Circle CenterX=58.0728 CenterY=73.3346 CenterZ=0 NormalX=0 NormalY=0 NormalZ=1 AngleXU=0 Radius=1
    g193: BSplineCurve PolesCount=3 KnotsCount=2 Degree=2 IsPeriodic=0
    g194: GeomPoint X=61.5791 Y=75.4095 Z=0
    g195: GeomPoint X=58.0728 Y=73.3346 Z=0
    g196: Circle CenterX=58.0728 CenterY=-40.8935 CenterZ=0 NormalX=0 NormalY=0 NormalZ=1 AngleXU=0 Radius=1
    g197: Circle CenterX=58.0728 CenterY=-44.8935 CenterZ=0 NormalX=0 NormalY=0 NormalZ=1 AngleXU=0 Radius=1
    g198: Circle CenterX=61.5791 CenterY=-42.9683 CenterZ=0 NormalX=0 NormalY=0 NormalZ=1 AngleXU=0 Radius=1
    g199: BSplineCurve PolesCount=3 KnotsCount=2 Degree=2 IsPeriodic=0
    g200: GeomPoint X=58.0728 Y=-40.8935 Z=0
    g201: GeomPoint X=61.5791 Y=-42.9683 Z=0
    g202: LineSegment StartX=61.5791 StartY=-42.9683 StartZ=0 EndX=165.871 EndY=14.2954 EndZ=0
    g203: LineSegment StartX=165.871 StartY=18.1458 StartZ=0 EndX=61.5791 EndY=75.4095 EndZ=0
    g204: LineSegment StartX=58.0728 StartY=73.3346 StartZ=0 EndX=58.0728 EndY=-40.8935 EndZ=0
    g205: Circle CenterX=302.567 CenterY=-42.9683 CenterZ=0 NormalX=0 NormalY=0 NormalZ=1 AngleXU=0 Radius=1
    g206: Circle CenterX=306.073 CenterY=-44.8935 CenterZ=0 NormalX=0 NormalY=0 NormalZ=1 AngleXU=0 Radius=1
    g207: Circle CenterX=306.073 CenterY=-40.8935 CenterZ=0 NormalX=0 NormalY=0 NormalZ=1 AngleXU=0 Radius=1
    g208: BSplineCurve PolesCount=3 KnotsCount=2 Degree=2 IsPeriodic=0
    g209: GeomPoint X=302.567 Y=-42.9683 Z=0
    g210: GeomPoint X=306.073 Y=-40.8935 Z=0
    g211: Circle CenterX=306.073 CenterY=73.3346 CenterZ=0 NormalX=0 NormalY=0 NormalZ=1 AngleXU=0 Radius=1
    g212: Circle CenterX=306.073 CenterY=77.3346 CenterZ=0 NormalX=0 NormalY=0 NormalZ=1 AngleXU=0 Radius=1
    g213: Circle CenterX=302.567 CenterY=75.4095 CenterZ=0 NormalX=0 NormalY=0 NormalZ=1 AngleXU=0 Radius=1
    g214: BSplineCurve PolesCount=3 KnotsCount=2 Degree=2 IsPeriodic=0
    g215: GeomPoint X=306.073 Y=73.3346 Z=0
    g216: GeomPoint X=302.567 Y=75.4095 Z=0
    g217: LineSegment StartX=302.567 StartY=-42.9683 StartZ=0 EndX=198.275 EndY=14.2954 EndZ=0
    g218: LineSegment StartX=198.275 StartY=18.1458 StartZ=0 EndX=302.567 EndY=75.4095 EndZ=0
    g219: LineSegment StartX=306.073 StartY=73.3346 StartZ=0 EndX=306.073 EndY=-40.8935 EndZ=0
    g220: LineSegment StartX=322.073 StartY=105.865 StartZ=0 EndX=328.643 EndY=105.865 EndZ=0
    g221: LineSegment StartX=318.073 StartY=120.221 StartZ=0 EndX=318.073 EndY=109.865 EndZ=0
    g222: LineSegment StartX=336.157 StartY=107.779 StartZ=0 EndX=362.567 EndY=122.294 EndZ=0
    g223: Circle CenterX=362.073 CenterY=124.221 CenterZ=0 NormalX=0 NormalY=0 NormalZ=1 AngleXU=0 Radius=1
    g224: Circle CenterX=366.073 CenterY=124.221 CenterZ=0 NormalX=0 NormalY=0 NormalZ=1 AngleXU=0 Radius=1
    g225: Circle CenterX=362.567 CenterY=122.294 CenterZ=0 NormalX=0 NormalY=0 NormalZ=1 AngleXU=0 Radius=1
    g226: BSplineCurve PolesCount=3 KnotsCount=2 Degree=2 IsPeriodic=0
    g227: GeomPoint X=362.073 Y=124.221 Z=0
    g228: GeomPoint X=362.567 Y=122.294 Z=0
    g229: Circle CenterX=322.073 CenterY=124.221 CenterZ=0 NormalX=0 NormalY=0 NormalZ=1 AngleXU=0 Radius=1
    g230: Circle CenterX=318.073 CenterY=124.221 CenterZ=0 NormalX=0 NormalY=0 NormalZ=1 AngleXU=0 Radius=1
    g231: Circle CenterX=318.073 CenterY=120.221 CenterZ=0 NormalX=0 NormalY=0 NormalZ=1 AngleXU=0 Radius=1
    g232: BSplineCurve PolesCount=3 KnotsCount=2 Degree=2 IsPeriodic=0
    g233: GeomPoint X=322.073 Y=124.221 Z=0
    g234: GeomPoint X=318.073 Y=120.221 Z=0
    g235: Circle CenterX=322.073 CenterY=105.865 CenterZ=0 NormalX=0 NormalY=0 NormalZ=1 AngleXU=0 Radius=1
    g236: Circle CenterX=318.073 CenterY=105.865 CenterZ=0 NormalX=0 NormalY=0 NormalZ=1 AngleXU=0 Radius=1
    g237: Circle CenterX=318.073 CenterY=109.865 CenterZ=0 NormalX=0 NormalY=0 NormalZ=1 AngleXU=0 Radius=1
    g238: BSplineCurve PolesCount=3 KnotsCount=2 Degree=2 IsPeriodic=0
    g239: GeomPoint X=322.073 Y=105.865 Z=0
    g240: GeomPoint X=318.073 Y=109.865 Z=0
    g241: Circle CenterX=336.157 CenterY=107.779 CenterZ=0 NormalX=0 NormalY=0 NormalZ=1 AngleXU=0 Radius=1
    g242: Circle CenterX=332.651 CenterY=105.853 CenterZ=0 NormalX=0 NormalY=0 NormalZ=1 AngleXU=0 Radius=1
    g243: Circle CenterX=328.643 CenterY=105.865 CenterZ=0 NormalX=0 NormalY=0 NormalZ=1 AngleXU=0 Radius=1
    g244: BSplineCurve PolesCount=3 KnotsCount=2 Degree=2 IsPeriodic=0
    g245: GeomPoint X=336.157 Y=107.779 Z=0
    g246: GeomPoint X=328.643 Y=105.865 Z=0
    g247: LineSegment StartX=322.073 StartY=124.221 StartZ=0 EndX=362.073 EndY=124.221 EndZ=0
    g248: Circle CenterX=371.567 CenterY=-80.8644 CenterZ=0 NormalX=0 NormalY=0 NormalZ=1 AngleXU=0 Radius=1
    g249: Circle CenterX=375.073 CenterY=-82.7896 CenterZ=0 NormalX=0 NormalY=0 NormalZ=1 AngleXU=0 Radius=1
    g250: Circle CenterX=375.073 CenterY=-78.7896 CenterZ=0 NormalX=0 NormalY=0 NormalZ=1 AngleXU=0 Radius=1
    g251: BSplineCurve PolesCount=3 KnotsCount=2 Degree=2 IsPeriodic=0
    g252: GeomPoint X=371.567 Y=-80.8644 Z=0
    g253: GeomPoint X=375.073 Y=-78.7896 Z=0
    g254: Circle CenterX=321.579 CenterY=-53.4075 CenterZ=0 NormalX=0 NormalY=0 NormalZ=1 AngleXU=0 Radius=1
    g255: Circle CenterX=318.073 CenterY=-51.4823 CenterZ=0 NormalX=0 NormalY=0 NormalZ=1 AngleXU=0 Radius=1
    g256: Circle CenterX=318.073 CenterY=-47.4805 CenterZ=0 NormalX=0 NormalY=0 NormalZ=1 AngleXU=0 Radius=1
    g257: BSplineCurve PolesCount=3 KnotsCount=2 Degree=2 IsPeriodic=0
    g258: GeomPoint X=321.579 Y=-53.4075 Z=0
    g259: GeomPoint X=318.073 Y=-47.4805 Z=0
    g260: LineSegment StartX=371.567 StartY=-80.8644 StartZ=0 EndX=321.579 EndY=-53.4075 EndZ=0
    g261: Circle CenterX=321.579 CenterY=-67.3492 CenterZ=0 NormalX=0 NormalY=0 NormalZ=1 AngleXU=0 Radius=1
    g262: Circle CenterX=318.073 CenterY=-65.424 CenterZ=0 NormalX=0 NormalY=0 NormalZ=1 AngleXU=0 Radius=1
    g263: Circle CenterX=318.073 CenterY=-69.424 CenterZ=0 NormalX=0 NormalY=0 NormalZ=1 AngleXU=0 Radius=1
    g264: BSplineCurve PolesCount=3 KnotsCount=2 Degree=2 IsPeriodic=0
    g265: GeomPoint X=321.579 Y=-67.3492 Z=0
    g266: GeomPoint X=318.073 Y=-69.424 Z=0
    g267: Circle CenterX=362.567 CenterY=-89.8542 CenterZ=0 NormalX=0 NormalY=0 NormalZ=1 AngleXU=0 Radius=1
    g268: Circle CenterX=366.073 CenterY=-91.7794 CenterZ=0 NormalX=0 NormalY=0 NormalZ=1 AngleXU=0 Radius=1
    g269: Circle CenterX=362.073 CenterY=-91.7794 CenterZ=0 NormalX=0 NormalY=0 NormalZ=1 AngleXU=0 Radius=1
    g270: BSplineCurve PolesCount=3 KnotsCount=2 Degree=2 IsPeriodic=0
    g271: GeomPoint X=362.567 Y=-89.8542 Z=0
    g272: GeomPoint X=362.073 Y=-91.7794 Z=0
    g273: Circle CenterX=322.073 CenterY=-91.7794 CenterZ=0 NormalX=0 NormalY=0 NormalZ=1 AngleXU=0 Radius=1
    g274: Circle CenterX=318.073 CenterY=-91.7794 CenterZ=0 NormalX=0 NormalY=0 NormalZ=1 AngleXU=0 Radius=1
    g275: Circle CenterX=318.073 CenterY=-87.7794 CenterZ=0 NormalX=0 NormalY=0 NormalZ=1 AngleXU=0 Radius=1
    g276: BSplineCurve PolesCount=3 KnotsCount=2 Degree=2 IsPeriodic=0
    g277: GeomPoint X=322.073 Y=-91.7794 Z=0
    g278: GeomPoint X=318.073 Y=-87.7794 Z=0
    g279: LineSegment StartX=362.567 StartY=-89.8542 StartZ=0 EndX=321.579 EndY=-67.3492 EndZ=0
    g280: LineSegment StartX=318.073 StartY=-69.424 StartZ=0 EndX=318.073 EndY=-87.7794 EndZ=0
    g281: LineSegment StartX=322.073 StartY=-91.7794 StartZ=0 EndX=362.073 EndY=-91.7794 EndZ=0
    g282: Circle CenterX=2.07281 CenterY=124.221 CenterZ=0 NormalX=0 NormalY=0 NormalZ=1 AngleXU=0 Radius=1
    g283: Circle CenterX=1.57905 CenterY=122.295 CenterZ=0 NormalX=0 NormalY=0 NormalZ=1 AngleXU=0 Radius=1
    g284: BSplineCurve PolesCount=3 KnotsCount=2 Degree=2 IsPeriodic=0
    g285: GeomPoint X=2.07281 Y=124.221 Z=0
    g286: GeomPoint X=1.57905 Y=122.295 Z=0
    g287: Circle CenterX=42.0728 CenterY=124.221 CenterZ=0 NormalX=0 NormalY=0 NormalZ=1 AngleXU=0 Radius=1
    g288: Circle CenterX=46.0728 CenterY=124.221 CenterZ=0 NormalX=0 NormalY=0 NormalZ=1 AngleXU=0 Radius=1
    g289: Circle CenterX=46.0728 CenterY=120.221 CenterZ=0 NormalX=0 NormalY=0 NormalZ=1 AngleXU=0 Radius=1
    g290: BSplineCurve PolesCount=3 KnotsCount=2 Degree=2 IsPeriodic=0
    g291: GeomPoint X=42.0728 Y=124.221 Z=0
    g292: GeomPoint X=46.0728 Y=120.221 Z=0
    g293: Circle CenterX=46.0728 CenterY=109.865 CenterZ=0 NormalX=0 NormalY=0 NormalZ=1 AngleXU=0 Radius=1
    g294: Circle CenterX=46.0728 CenterY=105.865 CenterZ=0 NormalX=0 NormalY=0 NormalZ=1 AngleXU=0 Radius=1
    g295: Circle CenterX=42.0728 CenterY=105.865 CenterZ=0 NormalX=0 NormalY=0 NormalZ=1 AngleXU=0 Radius=1
    g296: BSplineCurve PolesCount=3 KnotsCount=2 Degree=2 IsPeriodic=0
    g297: GeomPoint X=46.0728 Y=109.865 Z=0
    g298: GeomPoint X=42.0728 Y=105.865 Z=0
    g299: Circle CenterX=35.5028 CenterY=105.865 CenterZ=0 NormalX=0 NormalY=0 NormalZ=1 AngleXU=0 Radius=1
    g300: Circle CenterX=31.5028 CenterY=105.865 CenterZ=0 NormalX=0 NormalY=0 NormalZ=1 AngleXU=0 Radius=1
    g301: Circle CenterX=27.9965 CenterY=107.79 CenterZ=0 NormalX=0 NormalY=0 NormalZ=1 AngleXU=0 Radius=1
    g302: BSplineCurve PolesCount=3 KnotsCount=2 Degree=2 IsPeriodic=0
    g303: GeomPoint X=35.5028 Y=105.865 Z=0
    g304: GeomPoint X=27.9965 Y=107.79 Z=0
    g305: LineSegment StartX=2.07281 StartY=124.221 StartZ=0 EndX=42.0728 EndY=124.221 EndZ=0
    g306: LineSegment StartX=46.0728 StartY=120.221 StartZ=0 EndX=46.0728 EndY=109.865 EndZ=0
    g307: LineSegment StartX=42.0728 StartY=105.865 StartZ=0 EndX=35.5028 EndY=105.865 EndZ=0
    g308: LineSegment StartX=27.9965 StartY=107.79 StartZ=0 EndX=1.57905 EndY=122.295 EndZ=0
    g309: Circle CenterX=42.5666 CenterY=-67.3492 CenterZ=0 NormalX=0 NormalY=0 NormalZ=1 AngleXU=0 Radius=1
    g310: Circle CenterX=46.0728 CenterY=-65.424 CenterZ=0 NormalX=0 NormalY=0 NormalZ=1 AngleXU=0 Radius=1
    g311: Circle CenterX=46.0728 CenterY=-69.424 CenterZ=0 NormalX=0 NormalY=0 NormalZ=1 AngleXU=0 Radius=1
    g312: BSplineCurve PolesCount=3 KnotsCount=2 Degree=2 IsPeriodic=0
    g313: GeomPoint X=42.5666 Y=-67.3492 Z=0
    g314: GeomPoint X=46.0728 Y=-69.424 Z=0
    g315: Circle CenterX=46.0728 CenterY=-87.7794 CenterZ=0 NormalX=0 NormalY=0 NormalZ=1 AngleXU=0 Radius=1
    g316: Circle CenterX=46.0728 CenterY=-91.7794 CenterZ=0 NormalX=0 NormalY=0 NormalZ=1 AngleXU=0 Radius=1
    g317: Circle CenterX=42.0728 CenterY=-91.7794 CenterZ=0 NormalX=0 NormalY=0 NormalZ=1 AngleXU=0 Radius=1
    g318: BSplineCurve PolesCount=3 KnotsCount=2 Degree=2 IsPeriodic=0
    g319: GeomPoint X=46.0728 Y=-87.7794 Z=0
    g320: GeomPoint X=42.0728 Y=-91.7794 Z=0
    g321: Circle CenterX=2.07281 CenterY=-91.7794 CenterZ=0 NormalX=0 NormalY=0 NormalZ=1 AngleXU=0 Radius=1
    g322: Circle CenterX=-1.92719 CenterY=-91.7794 CenterZ=0 NormalX=0 NormalY=0 NormalZ=1 AngleXU=0 Radius=1
    g323: Circle CenterX=1.57905 CenterY=-89.8542 CenterZ=0 NormalX=0 NormalY=0 NormalZ=1 AngleXU=0 Radius=1
    g324: BSplineCurve PolesCount=3 KnotsCount=2 Degree=2 IsPeriodic=0
    g325: GeomPoint X=2.07281 Y=-91.7794 Z=0
    g326: GeomPoint X=1.57905 Y=-89.8542 Z=0
    g327: LineSegment StartX=2.07281 StartY=-91.7794 StartZ=0 EndX=42.0728 EndY=-91.7794 EndZ=0
    g328: LineSegment StartX=46.0728 StartY=-87.7794 StartZ=0 EndX=46.0728 EndY=-69.424 EndZ=0
    g329: LineSegment StartX=42.5666 StartY=-67.3492 StartZ=0 EndX=1.57905 EndY=-89.8542 EndZ=0
    g330: Circle CenterX=322.073 CenterY=76.4095 CenterZ=0 NormalX=0 NormalY=0 NormalZ=1 AngleXU=0 Radius=4
    g331: BSplineCurve PolesCount=3 KnotsCount=2 Degree=2 IsPeriodic=0
    g332: GeomPoint X=318.073 Y=72.4095 Z=0
    g333: GeomPoint X=322.073 Y=76.4095 Z=0
    g334: Circle CenterX=375.073 CenterY=72.4095 CenterZ=0 NormalX=0 NormalY=0 NormalZ=1 AngleXU=0 Radius=1
    g335: Circle CenterX=375.073 CenterY=76.4095 CenterZ=0 NormalX=0 NormalY=0 NormalZ=1 AngleXU=0 Radius=1
    g336: Circle CenterX=371.073 CenterY=76.4095 CenterZ=0 NormalX=0 NormalY=0 NormalZ=1 AngleXU=0 Radius=1
    g337: BSplineCurve PolesCount=3 KnotsCount=2 Degree=2 IsPeriodic=0
    g338: GeomPoint X=375.073 Y=72.4095 Z=0
    g339: GeomPoint X=371.073 Y=76.4095 Z=0
    g340: LineSegment StartX=322.073 StartY=76.4095 StartZ=0 EndX=371.073 EndY=76.4095 EndZ=0
    g341: LineSegment StartX=318.073 StartY=72.4095 StartZ=0 EndX=318.073 EndY=-47.4805 EndZ=0
    g342: LineSegment StartX=375.073 StartY=72.4095 StartZ=0 EndX=375.073 EndY=-78.7896 EndZ=0
    g343: ArcOfCircle CenterX=-26.9272 CenterY=22.1087 CenterZ=0 NormalX=0 NormalY=0 NormalZ=1 AngleXU=0 Radius=4 StartAngle=5e-16 EndAngle=3.14159
    g344: LineSegment StartX=-22.9272 StartY=22.1087 StartZ=0 EndX=-18.9272 EndY=-83.7794 EndZ=0
    g345: LineSegment StartX=-34.9272 StartY=-83.7794 StartZ=0 EndX=-30.9272 EndY=22.1087 EndZ=0
    g346: ArcOfCircle CenterX=391.073 CenterY=22.1087 CenterZ=0 NormalX=0 NormalY=0 NormalZ=1 AngleXU=0 Radius=4 StartAngle=0 EndAngle=3.14159
    g347: LineSegment StartX=387.073 StartY=22.1087 StartZ=0 EndX=383.073 EndY=-83.7794 EndZ=0
    g348: LineSegment StartX=395.073 StartY=22.1087 StartZ=0 EndX=399.073 EndY=-83.7794 EndZ=0
    g349: LineSegment StartX=-10.9272 StartY=76.4095 StartZ=0 EndX=-6.92718 EndY=76.4095 EndZ=0
    g350: LineSegment StartX=-10.9272 StartY=76.4095 StartZ=0 EndX=-10.9272 EndY=72.4095 EndZ=0
    g351: LineSegment StartX=46.0728 StartY=76.4095 StartZ=0 EndX=42.0728 EndY=76.4095 EndZ=0
    g352: LineSegment StartX=46.0728 StartY=76.4095 StartZ=0 EndX=46.0728 EndY=72.4095 EndZ=0
    g353: LineSegment StartX=46.0728 StartY=-51.4823 StartZ=0 EndX=46.0728 EndY=-47.4823 EndZ=0
    g354: LineSegment StartX=46.0728 StartY=-51.4823 StartZ=0 EndX=42.5666 EndY=-53.4075 EndZ=0
    g355: LineSegment StartX=-10.9272 StartY=-82.7794 StartZ=0 EndX=-7.42095 EndY=-80.8542 EndZ=0
    g356: LineSegment StartX=-10.9272 StartY=-82.7794 StartZ=0 EndX=-10.9272 EndY=-78.7794 EndZ=0
    g357: Circle CenterX=-10.9272 CenterY=-78.7794 CenterZ=0 NormalX=0 NormalY=0 NormalZ=1 AngleXU=0 Radius=1
    g358: Circle CenterX=-10.9272 CenterY=-82.7794 CenterZ=0 NormalX=0 NormalY=0 NormalZ=1 AngleXU=0 Radius=1
    g359: Circle CenterX=-7.42095 CenterY=-80.8542 CenterZ=0 NormalX=0 NormalY=0 NormalZ=1 AngleXU=0 Radius=1
    g360: BSplineCurve PolesCount=3 KnotsCount=2 Degree=2 IsPeriodic=0
    g361: GeomPoint X=-10.9272 Y=-78.7794 Z=0
    g362: GeomPoint X=-7.42095 Y=-80.8542 Z=0
    g363: Circle CenterX=42.5666 CenterY=-53.4075 CenterZ=0 NormalX=0 NormalY=0 NormalZ=1 AngleXU=0 Radius=1
    g364: Circle CenterX=46.0728 CenterY=-51.4823 CenterZ=0 NormalX=0 NormalY=0 NormalZ=1 AngleXU=0 Radius=1
    g365: Circle CenterX=46.0728 CenterY=-47.4823 CenterZ=0 NormalX=0 NormalY=0 NormalZ=1 AngleXU=0 Radius=1
    g366: BSplineCurve PolesCount=3 KnotsCount=2 Degree=2 IsPeriodic=0
    g367: GeomPoint X=42.5666 Y=-53.4075 Z=0
    g368: GeomPoint X=46.0728 Y=-47.4823 Z=0
    g369: Circle CenterX=46.0728 CenterY=72.4095 CenterZ=0 NormalX=0 NormalY=0 NormalZ=1 AngleXU=0 Radius=1
    g370: Circle CenterX=46.0728 CenterY=76.4095 CenterZ=0 NormalX=0 NormalY=0 NormalZ=1 AngleXU=0 Radius=1
    g371: Circle CenterX=42.0728 CenterY=76.4095 CenterZ=0 NormalX=0 NormalY=0 NormalZ=1 AngleXU=0 Radius=1
    g372: BSplineCurve PolesCount=3 KnotsCount=2 Degree=2 IsPeriodic=0
    g373: GeomPoint X=46.0728 Y=72.4095 Z=0
    g374: GeomPoint X=42.0728 Y=76.4095 Z=0
    g375: Circle CenterX=-6.92718 CenterY=76.4095 CenterZ=0 NormalX=0 NormalY=0 NormalZ=1 AngleXU=0 Radius=1
    g376: Circle CenterX=-10.9272 CenterY=76.4095 CenterZ=0 NormalX=0 NormalY=0 NormalZ=1 AngleXU=0 Radius=1
    g377: Circle CenterX=-10.9272 CenterY=72.4095 CenterZ=0 NormalX=0 NormalY=0 NormalZ=1 AngleXU=0 Radius=1
    g378: BSplineCurve PolesCount=3 KnotsCount=2 Degree=2 IsPeriodic=0
    g379: GeomPoint X=-6.92718 Y=76.4095 Z=0
    g380: GeomPoint X=-10.9272 Y=72.4095 Z=0
  constraints (641):
    c: Coincident(g0,g2)
    c: Block(g0)
    c: Block(g1)
    c: Vertical(g3)
    c: Vertical(g4)
    c: Block(g4)
    c: Block(g3)
    c: Weight(g7) = 1
    c: Equal(g7,g8)
    c: Equal(g7,g9)
    c: InternalAlignment(g7,g10)
    c: InternalAlignment(g8,g10)
    c: InternalAlignment(g9,g10)
    c: InternalAlignment(g11,g10)
    c: InternalAlignment(g12,g10)
    c: Weight(g13) = 1
    c: Equal(g13,g14)
    c: Equal(g13,g15)
    c: InternalAlignment(g13,g16)
    c: InternalAlignment(g14,g16)
    c: InternalAlignment(g15,g16)
    c: InternalAlignment(g17,g16)
    c: InternalAlignment(g18,g16)
    c: Block(g16)
    c: Block(g10)
    c: Weight(g19) = 1
    c: Equal(g19,g20)
    c: Equal(g19,g21)
    c: InternalAlignment(g19,g22)
    c: InternalAlignment(g20,g22)
    c: InternalAlignment(g21,g22)
    c: InternalAlignment(g23,g22)
    c: InternalAlignment(g24,g22)
    c: Weight(g25) = 1
    c: Equal(g25,g26)
    c: Equal(g25,g27)
    c: InternalAlignment(g25,g28)
    c: InternalAlignment(g26,g28)
    c: InternalAlignment(g27,g28)
    c: InternalAlignment(g29,g28)
    c: InternalAlignment(g30,g28)
    c: Block(g28)
    c: Block(g22)
    c: Weight(g31) = 1
    c: Equal(g31,g32)
    c: Equal(g31,g33)
    c: InternalAlignment(g31,g34)
    c: InternalAlignment(g32,g34)
    c: InternalAlignment(g33,g34)
    c: InternalAlignment(g35,g34)
    c: InternalAlignment(g36,g34)
    c: Weight(g37) = 1
    c: Equal(g37,g38)
    c: Equal(g37,g39)
    c: InternalAlignment(g37,g40)
    c: InternalAlignment(g38,g40)
    c: InternalAlignment(g39,g40)
    c: InternalAlignment(g41,g40)
    c: InternalAlignment(g42,g40)
    c: Block(g34)
    c: Block(g40)
    c: Coincident(g43,g4)
    c: Coincident(g43,g3)
    c: Horizontal(g43)
    c: Distance(g43) = 450
    c: Coincident(g44,g4)
    c: Coincident(g44,g3)
    c: Horizontal(g44)
    c: Horizontal(g45)
    c: Coincident(g2,g45)
    c: Block(g45)
    c: Coincident(g1,g45)
    c: Weight(g46) = 1
    c: Equal(g46,g47)
    c: Equal(g46,g48)
    c: InternalAlignment(g46,g49)
    c: InternalAlignment(g47,g49)
    c: InternalAlignment(g48,g49)
    c: InternalAlignment(g50,g49)
    c: InternalAlignment(g51,g49)
    c: Block(g49)
    c: Weight(g52) = 1
    c: Equal(g52,g53)
    c: Equal(g52,g54)
    c: InternalAlignment(g52,g55)
    c: InternalAlignment(g53,g55)
    c: InternalAlignment(g54,g55)
    c: InternalAlignment(g56,g55)
    c: InternalAlignment(g57,g55)
    c: Block(g55)
    c: Weight(g58) = 1
    c: Equal(g58,g59)
    c: Equal(g58,g60)
    c: InternalAlignment(g58,g61)
    c: InternalAlignment(g59,g61)
    c: InternalAlignment(g60,g61)
    c: InternalAlignment(g62,g61)
    c: InternalAlignment(g63,g61)
    c: Block(g61)
    c: Weight(g64) = 1
    c: Equal(g64,g65)
    c: Equal(g64,g66)
    c: InternalAlignment(g64,g67)
    c: InternalAlignment(g65,g67)
    c: InternalAlignment(g66,g67)
    c: InternalAlignment(g68,g67)
    c: InternalAlignment(g69,g67)
    c: Block(g67)
    c: Weight(g70) = 1
    c: Equal(g70,g71)
    c: Equal(g70,g72)
    c: InternalAlignment(g70,g73)
    c: InternalAlignment(g71,g73)
    c: InternalAlignment(g72,g73)
    c: InternalAlignment(g74,g73)
    c: InternalAlignment(g75,g73)
    c: Weight(g76) = 1
    c: Equal(g76,g77)
    c: Equal(g76,g78)
    c: InternalAlignment(g76,g79)
    c: InternalAlignment(g77,g79)
    c: InternalAlignment(g78,g79)
    c: InternalAlignment(g80,g79)
    c: InternalAlignment(g81,g79)
    c: Block(g73)
    c: Block(g79)
    c: Coincident(g82,g73)
    c: Coincident(g82,g79)
    c: Vertical(g82)
    c: Coincident(g83,g73)
    c: Coincident(g83,g55)
    c: Coincident(g84,g55)
    c: Coincident(g84,g79)
    c: Weight(g85) = 1
    c: Equal(g85,g86)
    c: Equal(g85,g87)
    c: InternalAlignment(g85,g88)
    c: InternalAlignment(g86,g88)
    c: InternalAlignment(g87,g88)
    c: InternalAlignment(g89,g88)
    c: InternalAlignment(g90,g88)
    c: Weight(g91) = 1
    c: Equal(g91,g92)
    c: Equal(g91,g93)
    c: InternalAlignment(g91,g94)
    c: InternalAlignment(g92,g94)
    c: InternalAlignment(g93,g94)
    c: InternalAlignment(g95,g94)
    c: InternalAlignment(g96,g94)
    c: Block(g88)
    c: Block(g94)
    c: Coincident(g97,g88)
    c: Coincident(g97,g94)
    c: Vertical(g97)
    c: Coincident(g98,g88)
    c: Coincident(g98,g49)
    c: Coincident(g99,g49)
    c: Coincident(g99,g94)
    c: Weight(g100) = 1
    c: Equal(g100,g101)
    c: Equal(g100,g102)
    c: InternalAlignment(g100,g103)
    c: InternalAlignment(g101,g103)
    c: InternalAlignment(g102,g103)
    c: InternalAlignment(g104,g103)
    c: InternalAlignment(g105,g103)
    c: Weight(g106) = 1
    c: Equal(g106,g107)
    c: Equal(g106,g108)
    c: InternalAlignment(g106,g109)
    c: InternalAlignment(g107,g109)
    c: InternalAlignment(g108,g109)
    c: InternalAlignment(g110,g109)
    c: InternalAlignment(g111,g109)
    c: Block(g103)
    c: Block(g109)
    c: Coincident(g112,g103)
    c: Coincident(g112,g109)
    c: Vertical(g112)
    c: Coincident(g113,g109)
    c: Coincident(g113,g67)
    c: Coincident(g114,g67)
    c: Coincident(g114,g103)
    c: Weight(g115) = 1
    c: Equal(g115,g116)
    c: Equal(g115,g117)
    c: InternalAlignment(g115,g118)
    c: InternalAlignment(g116,g118)
    c: InternalAlignment(g117,g118)
    c: InternalAlignment(g119,g118)
    c: InternalAlignment(g120,g118)
    c: Weight(g121) = 1
    c: Equal(g121,g122)
    c: Equal(g121,g123)
    c: InternalAlignment(g121,g124)
    c: InternalAlignment(g122,g124)
    c: InternalAlignment(g123,g124)
    c: InternalAlignment(g125,g124)
    c: InternalAlignment(g126,g124)
    c: Block(g118)
    c: Block(g124)
    c: Coincident(g127,g118)
    c: Coincident(g127,g124)
    c: Vertical(g127)
    c: Coincident(g128,g124)
    c: Coincident(g128,g61)
    c: Coincident(g129,g61)
    c: Coincident(g129,g118)
    c: Weight(g130) = 1
    c: Equal(g130,g131)
    c: Equal(g130,g132)
    c: InternalAlignment(g130,g133)
    c: InternalAlignment(g131,g133)
    c: InternalAlignment(g132,g133)
    c: InternalAlignment(g134,g133)
    c: InternalAlignment(g135,g133)
    c: Weight(g136) = 1
    c: Equal(g136,g137)
    c: Equal(g136,g138)
    c: InternalAlignment(g136,g139)
    c: InternalAlignment(g137,g139)
    c: InternalAlignment(g138,g139)
    c: InternalAlignment(g140,g139)
    c: InternalAlignment(g141,g139)
    c: Weight(g142) = 1
    c: Equal(g142,g143)
    c: Equal(g142,g144)
    c: InternalAlignment(g142,g145)
    c: InternalAlignment(g143,g145)
    c: InternalAlignment(g144,g145)
    c: InternalAlignment(g146,g145)
    c: InternalAlignment(g147,g145)
    c: Weight(g148) = 1
    c: Equal(g148,g149)
    c: Equal(g148,g150)
    c: InternalAlignment(g148,g151)
    c: InternalAlignment(g149,g151)
    c: InternalAlignment(g150,g151)
    c: InternalAlignment(g152,g151)
    c: InternalAlignment(g153,g151)
    c: Block(g151)
    c: Block(g145)
    c: Block(g139)
    c: Block(g133)
    c: Coincident(g154,g28)
    c: Coincident(g154,g151)
    c: Coincident(g155,g151)
    c: Coincident(g155,g145)
    c: Horizontal(g155)
    c: Coincident(g156,g145)
    c: Coincident(g156,g28)
    c: Vertical(g156)
    c: Coincident(g157,g22)
    c: Coincident(g157,g139)
    c: Vertical(g157)
    c: Coincident(g158,g139)
    c: Coincident(g158,g133)
    c: Horizontal(g158)
    c: Coincident(g159,g133)
    c: Coincident(g159,g22)
    c: Weight(g160) = 1
    c: Equal(g160,g161)
    c: Equal(g160,g162)
    c: InternalAlignment(g160,g163)
    c: InternalAlignment(g161,g163)
    c: InternalAlignment(g162,g163)
    c: InternalAlignment(g164,g163)
    c: InternalAlignment(g165,g163)
    c: Weight(g166) = 1
    c: Equal(g166,g167)
    c: Equal(g166,g168)
    c: InternalAlignment(g166,g169)
    c: InternalAlignment(g167,g169)
    c: InternalAlignment(g168,g169)
    c: InternalAlignment(g170,g169)
    c: InternalAlignment(g171,g169)
    c: Weight(g172) = 1
    c: Equal(g172,g173)
    c: Equal(g172,g174)
    c: InternalAlignment(g172,g175)
    c: InternalAlignment(g173,g175)
    c: InternalAlignment(g174,g175)
    c: InternalAlignment(g176,g175)
    c: InternalAlignment(g177,g175)
    c: Weight(g178) = 1
    c: Equal(g178,g179)
    c: Equal(g178,g180)
    c: InternalAlignment(g178,g181)
    c: InternalAlignment(g179,g181)
    c: InternalAlignment(g180,g181)
    c: InternalAlignment(g182,g181)
    c: InternalAlignment(g183,g181)
    c: Block(g181)
    c: Block(g175)
    c: Block(g169)
    c: Block(g163)
    c: Coincident(g184,g181)
    c: Coincident(g184,g175)
    c: Horizontal(g184)
    c: Coincident(g185,g175)
    c: Coincident(g185,g10)
    c: Vertical(g185)
    c: Coincident(g186,g16)
    c: Coincident(g186,g169)
    c: Vertical(g186)
    c: Coincident(g187,g169)
    c: Coincident(g187,g163)
    c: Horizontal(g187)
    c: Coincident(g188,g163)
    c: Coincident(g188,g16)
    c: Coincident(g189,g10)
    c: Weight(g190) = 1
    c: Equal(g190,g191)
    c: Equal(g190,g192)
    c: InternalAlignment(g190,g193)
    c: InternalAlignment(g191,g193)
    c: InternalAlignment(g192,g193)
    c: InternalAlignment(g194,g193)
    c: InternalAlignment(g195,g193)
    c: Weight(g196) = 1
    c: Equal(g196,g197)
    c: Equal(g196,g198)
    c: InternalAlignment(g196,g199)
    c: InternalAlignment(g197,g199)
    c: InternalAlignment(g198,g199)
    c: InternalAlignment(g200,g199)
    c: InternalAlignment(g201,g199)
    c: Block(g199)
    c: Block(g193)
    c: Coincident(g202,g199)
    c: Coincident(g202,g34)
    c: Coincident(g203,g34)
    c: Coincident(g203,g193)
    c: Coincident(g204,g193)
    c: Coincident(g204,g199)
    c: Vertical(g204)
    c: Weight(g205) = 1
    c: Equal(g205,g206)
    c: Equal(g205,g207)
    c: InternalAlignment(g205,g208)
    c: InternalAlignment(g206,g208)
    c: InternalAlignment(g207,g208)
    c: InternalAlignment(g209,g208)
    c: InternalAlignment(g210,g208)
    c: Weight(g211) = 1
    c: Equal(g211,g212)
    c: Equal(g211,g213)
    c: InternalAlignment(g211,g214)
    c: InternalAlignment(g212,g214)
    c: InternalAlignment(g213,g214)
    c: InternalAlignment(g215,g214)
    c: InternalAlignment(g216,g214)
    c: Block(g214)
    c: Block(g208)
    c: Coincident(g217,g208)
    c: Coincident(g217,g40)
    c: Coincident(g218,g40)
    c: Coincident(g218,g214)
    c: Coincident(g219,g214)
    c: Coincident(g219,g208)
    c: Vertical(g219)
    c: Horizontal(g220)
    c: Block(g220)
    c: Vertical(g221)
    c: Block(g221)
    c: Block(g222)
    c: Weight(g223) = 1
    c: Equal(g223,g224)
    c: Equal(g223,g225)
    c: InternalAlignment(g223,g226)
    c: InternalAlignment(g224,g226)
    c: InternalAlignment(g225,g226)
    c: InternalAlignment(g227,g226)
    c: InternalAlignment(g228,g226)
    c: Weight(g229) = 1
    c: Equal(g229,g230)
    c: Equal(g229,g231)
    c: InternalAlignment(g229,g232)
    c: InternalAlignment(g230,g232)
    c: InternalAlignment(g231,g232)
    c: InternalAlignment(g233,g232)
    c: InternalAlignment(g234,g232)
    c: Weight(g235) = 1
    c: Equal(g235,g236)
    c: Equal(g235,g237)
    c: InternalAlignment(g235,g238)
    c: InternalAlignment(g236,g238)
    c: InternalAlignment(g237,g238)
    c: InternalAlignment(g239,g238)
    c: InternalAlignment(g240,g238)
    c: Weight(g241) = 1
    c: Equal(g241,g242)
    c: Equal(g241,g243)
    c: InternalAlignment(g241,g244)
    c: InternalAlignment(g242,g244)
    c: InternalAlignment(g243,g244)
    c: InternalAlignment(g245,g244)
    c: InternalAlignment(g246,g244)
    c: Block(g226)
    c: Block(g232)
    c: Block(g238)
    c: Block(g244)
    c: Coincident(g247,g232)
    c: Coincident(g247,g226)
    c: Horizontal(g247)
    c: Block(g189)
    c: Weight(g248) = 1
    c: Equal(g248,g249)
    c: Equal(g248,g250)
    c: InternalAlignment(g248,g251)
    c: InternalAlignment(g249,g251)
    c: InternalAlignment(g250,g251)
    c: InternalAlignment(g252,g251)
    c: InternalAlignment(g253,g251)
    c: Weight(g254) = 1
    c: Equal(g254,g255)
    c: Equal(g254,g256)
    c: InternalAlignment(g254,g257)
    c: InternalAlignment(g255,g257)
    c: InternalAlignment(g256,g257)
    c: InternalAlignment(g258,g257)
    c: InternalAlignment(g259,g257)
    c: Block(g251)
    c: Block(g257)
    c: Coincident(g260,g251)
    c: Coincident(g260,g257)
    c: Weight(g261) = 1
    c: Equal(g261,g262)
    c: Equal(g261,g263)
    c: InternalAlignment(g261,g264)
    c: InternalAlignment(g262,g264)
    c: InternalAlignment(g263,g264)
    c: InternalAlignment(g265,g264)
    c: InternalAlignment(g266,g264)
    c: Weight(g267) = 1
    c: Equal(g267,g268)
    c: Equal(g267,g269)
    c: InternalAlignment(g267,g270)
    c: InternalAlignment(g268,g270)
    c: InternalAlignment(g269,g270)
    c: InternalAlignment(g271,g270)
    c: InternalAlignment(g272,g270)
    c: Weight(g273) = 1
    c: Equal(g273,g274)
    c: Equal(g273,g275)
    c: InternalAlignment(g273,g276)
    c: InternalAlignment(g274,g276)
    c: InternalAlignment(g275,g276)
    c: InternalAlignment(g277,g276)
    c: InternalAlignment(g278,g276)
    c: Block(g276)
    c: Block(g270)
    c: Block(g264)
    c: Coincident(g279,g270)
    c: Coincident(g279,g264)
    c: Coincident(g280,g264)
    c: Coincident(g280,g276)
    c: Vertical(g280)
    c: Coincident(g281,g276)
    c: Coincident(g281,g270)
    c: Horizontal(g281)
    c: Weight(g282) = 1
    c: Equal(g282,g283)
    c: InternalAlignment(g282,g284)
    c: InternalAlignment(g283,g284)
    c: InternalAlignment(g285,g284)
    c: InternalAlignment(g286,g284)
    c: Weight(g287) = 1
    c: InternalAlignment(g288,g290)
    c: InternalAlignment(g289,g290)
    c: InternalAlignment(g291,g290)
    c: InternalAlignment(g292,g290)
    c: Weight(g293) = 1
    c: Equal(g293,g294)
    c: Equal(g293,g295)
    c: InternalAlignment(g293,g296)
    c: InternalAlignment(g294,g296)
    c: InternalAlignment(g295,g296)
    c: InternalAlignment(g297,g296)
    c: InternalAlignment(g298,g296)
    c: Equal(g299,g300)
    c: Equal(g299,g301)
    c: InternalAlignment(g299,g302)
    c: InternalAlignment(g300,g302)
    c: InternalAlignment(g301,g302)
    c: InternalAlignment(g303,g302)
    c: InternalAlignment(g304,g302)
    c: Block(g290)
    c: Block(g296)
    c: Block(g302)
    c: Block(g284)
    c: Coincident(g305,g284)
    c: Coincident(g305,g290)
    c: Horizontal(g305)
    c: Coincident(g306,g290)
    c: Coincident(g306,g296)
    c: Vertical(g306)
    c: Coincident(g307,g296)
    c: Coincident(g307,g302)
    c: Horizontal(g307)
    c: Coincident(g308,g302)
    c: Coincident(g308,g284)
    c: Weight(g309) = 1
    c: Equal(g309,g310)
    c: Equal(g309,g311)
    c: InternalAlignment(g309,g312)
    c: InternalAlignment(g310,g312)
    c: InternalAlignment(g311,g312)
    c: InternalAlignment(g313,g312)
    c: InternalAlignment(g314,g312)
    c: Weight(g315) = 1
    c: Equal(g315,g316)
    c: Equal(g315,g317)
    c: InternalAlignment(g315,g318)
    c: InternalAlignment(g316,g318)
    c: InternalAlignment(g317,g318)
    c: InternalAlignment(g319,g318)
    c: InternalAlignment(g320,g318)
    c: Weight(g321) = 1
    c: Equal(g321,g322)
    c: Equal(g321,g323)
    c: InternalAlignment(g321,g324)
    c: InternalAlignment(g322,g324)
    c: InternalAlignment(g323,g324)
    c: InternalAlignment(g325,g324)
    c: InternalAlignment(g326,g324)
    c: Block(g324)
    c: Block(g318)
    c: Block(g312)
    c: Coincident(g327,g324)
    c: Coincident(g327,g318)
    c: Horizontal(g327)
    c: Coincident(g328,g318)
    c: Coincident(g328,g312)
    c: Vertical(g328)
    c: Coincident(g329,g312)
    c: Coincident(g329,g324)
    c: InternalAlignment(g330,g331)
    c: InternalAlignment(g332,g331)
    c: InternalAlignment(g333,g331)
    c: Block(g331)
    c: Equal(g334,g335)
    c: Equal(g334,g336)
    c: InternalAlignment(g334,g337)
    c: InternalAlignment(g335,g337)
    c: InternalAlignment(g336,g337)
    c: InternalAlignment(g338,g337)
    c: InternalAlignment(g339,g337)
    c: Block(g337)
    c: Coincident(g340,g331)
    c: Horizontal(g340)
    c: Block(g340)
    c: Coincident(g341,g331)
    c: Coincident(g341,g257)
    c: Vertical(g341)
    c: Coincident(g342,g337)
    c: Coincident(g342,g251)
    c: Vertical(g342)
    c: Block(g343)
    c: Block(g5)
    c: Distance(g341) = 119.89
    c: Coincident(g344,g343)
    c: Coincident(g344,g5)
    c: Coincident(g345,g5)
    c: Coincident(g345,g343)
    c: Block(g6)
    c: Block(g346)
    c: Coincident(g347,g346)
    c: Coincident(g347,g6)
    c: Coincident(g348,g346)
    c: Coincident(g348,g6)
    c: Block(g348)
    c: Block(g347)
    c: Horizontal(g349)
    c: Vertical(g350)
    c: Horizontal(g351)
    c: Vertical(g352)
    c: Vertical(g353)
    c: Vertical(g356)
    c: Parallel(g0,g355)
    c: Parallel(g354,g0)
    c: Distance(g354) = 4
    c: Distance(g353) = 4
    c: Distance(g355) = 4
    c: Distance(g356) = 4
    c: Distance(g349) = 4
    c: Distance(g350) = 4
    c: Distance(g351) = 4
    c: Distance(g352) = 4
    c: Coincident(g349,g1)
    c: Coincident(g350,g1)
    c: Coincident(g352,g2)
    c: Coincident(g351,g2)
    c: Coincident(g353,g0)
    c: Coincident(g354,g0)
    c: Coincident(g355,g0)
    c: Coincident(g356,g0)
    c: Coincident(g360,g356)
    c: Weight(g357) = 1
    c: Equal(g357,g358)
    c: Coincident(g358,g0)
    c: Equal(g357,g359)
    c: Coincident(g360,g355)
    c: InternalAlignment(g357,g360)
    c: InternalAlignment(g358,g360)
    c: InternalAlignment(g359,g360)
    c: InternalAlignment(g361,g360)
    c: InternalAlignment(g362,g360)
    c: Coincident(g366,g354)
    c: Weight(g363) = 1
    c: Equal(g363,g364)
    c: Coincident(g364,g0)
    c: Equal(g363,g365)
    c: Coincident(g366,g353)
    c: InternalAlignment(g363,g366)
    c: InternalAlignment(g364,g366)
    c: InternalAlignment(g365,g366)
    c: InternalAlignment(g367,g366)
    c: InternalAlignment(g368,g366)
    c: Coincident(g372,g352)
    c: Weight(g369) = 1
    c: Equal(g369,g370)
    c: Coincident(g370,g2)
    c: Equal(g369,g371)
    c: Coincident(g372,g351)
    c: InternalAlignment(g369,g372)
    c: InternalAlignment(g370,g372)
    c: InternalAlignment(g371,g372)
    c: InternalAlignment(g373,g372)
    c: InternalAlignment(g374,g372)
    c: Coincident(g378,g349)
    c: Weight(g375) = 1
    c: Equal(g375,g376)
    c: Coincident(g376,g1)
    c: Equal(g375,g377)
    c: Coincident(g378,g350)
    c: InternalAlignment(g375,g378)
    c: InternalAlignment(g376,g378)
    c: InternalAlignment(g377,g378)
    c: InternalAlignment(g379,g378)
    c: InternalAlignment(g380,g378)
